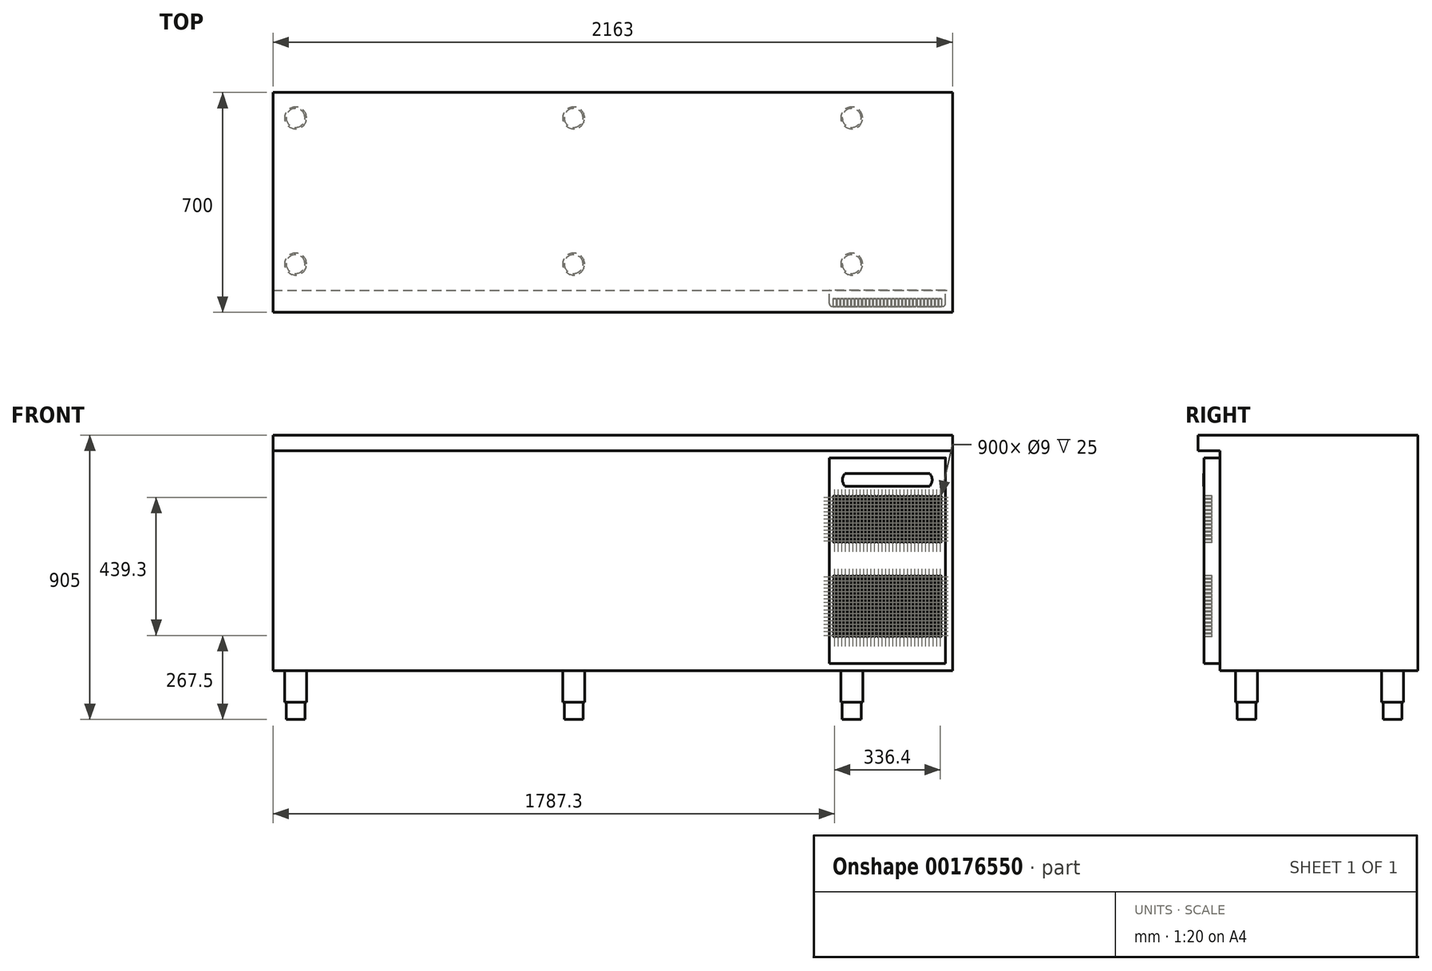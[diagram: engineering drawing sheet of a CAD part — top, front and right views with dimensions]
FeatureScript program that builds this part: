
annotation { "Feature Type Name" : "Feature", "Feature Type Description" : "" }
export const myFeature = defineFeature(function(context is Context, id is Id, definition is map)
    precondition{}
    {
        {
            var Q0;
            Q0=qCreatedBy(makeId("Top.planeOp"),FACE);
            var sketch = newSketch(context, id + "F0", { "sketchPlane" : qUnion([Q0])});
            skLineSegment(sketch, "E0.bottom", {"start": v(1081.5, 350) * mm, "end": v(-1081.5, 350) * mm});
            skLineSegment(sketch, "E0.top", {"start": v(1081.5, -350) * mm, "end": v(-1081.5, -350) * mm});
            skLineSegment(sketch, "E0.left", {"start": v(1081.5, 350) * mm, "end": v(1081.5, -350) * mm});
            skLineSegment(sketch, "E0.right", {"start": v(-1081.5, 350) * mm, "end": v(-1081.5, -350) * mm});
            skPoint(sketch, "E0.middle", {"position": v(0, 0) * mm});
            skSolve(sketch);
        }
        {
            var Q0;
            Q0 = qSketchRegion(id + "F0", true);
            extrude(context, id + "F1", {"entities" : qUnion([Q0]), "depth" : 50 * mm});
        }
        {
            var Q0;
            Q0=makeQuery(id+"F1.opExtrude","CAP_FACE",FACE,{"disambiguationData":[OSD([sQuery(id+"F0.wireOp",EDGE,"E0.bottom"),sQuery(id+"F0.wireOp",EDGE,"E0.top"),sQuery(id+"F0.wireOp",EDGE,"E0.left"),sQuery(id+"F0.wireOp",EDGE,"E0.right")])],"isStart":true});
            var sketch = newSketch(context, id + "F2", { "sketchPlane" : qUnion([Q0])});
            skLineSegment(sketch, "E1.bottom", {"start": v(-1081.5, -350) * mm, "end": v(1081.5, -350) * mm});
            skLineSegment(sketch, "E1.top", {"start": v(-1081.5, 280) * mm, "end": v(1081.5, 280) * mm});
            skLineSegment(sketch, "E1.left", {"start": v(-1081.5, -350) * mm, "end": v(-1081.5, 280) * mm});
            skLineSegment(sketch, "E1.right", {"start": v(1081.5, -350) * mm, "end": v(1081.5, 280) * mm});
            skSolve(sketch);
        }
        {
            var Q0;
            Q0 = qSketchRegion(id + "F2", true);
            extrude(context, id + "F3", {"entities" : qUnion([Q0]), "operationType" : NewBodyOperationType.ADD, "depth" : 700 * mm});
        }
        {
            var Q0;
            Q0=makeQuery(id+"F3.opExtrude","CAP_FACE",FACE,{"disambiguationData":[OSD([sQuery(id+"F2.wireOp",EDGE,"E1.bottom"),sQuery(id+"F2.wireOp",EDGE,"E1.top"),sQuery(id+"F2.wireOp",EDGE,"E1.left"),sQuery(id+"F2.wireOp",EDGE,"E1.right")])],"isStart":false});
            var sketch = newSketch(context, id + "F4", { "sketchPlane" : qUnion([Q0])});
            skCircle(sketch, "E2", {"center": v(-1009.5, 196) * mm, "radius": 35 * mm});
            skCircle(sketch, "E3", {"center": v(-124.5, 196) * mm, "radius": 35 * mm});
            skCircle(sketch, "E4", {"center": v(760.5, 196) * mm, "radius": 35 * mm});
            skCircle(sketch, "E5", {"center": v(760.5, -269) * mm, "radius": 35 * mm});
            skCircle(sketch, "E6", {"center": v(-124.5, -269) * mm, "radius": 35 * mm});
            skCircle(sketch, "E7", {"center": v(-1009.5, -269) * mm, "radius": 35 * mm});
            skSolve(sketch);
        }
        {
            var Q0;
            Q0 = qSketchRegion(id + "F4", true);
            extrude(context, id + "F5", {"entities" : qUnion([Q0]), "operationType" : NewBodyOperationType.ADD, "depth" : 100 * mm});
        }
        {
            var Q0;
            Q0=makeQuery(id+"F5.opExtrude","CAP_FACE",FACE,{"disambiguationData":[OSD([sQuery(id+"F4.wireOp",EDGE,"E2")])],"isStart":false});
            var sketch = newSketch(context, id + "F6", { "sketchPlane" : qUnion([Q0])});
            skCircle(sketch, "E8", {"center": v(-1009.5, 196) * mm, "radius": 30 * mm});
            skCircle(sketch, "E9", {"center": v(-124.5, 196) * mm, "radius": 30 * mm});
            skCircle(sketch, "E10", {"center": v(760.5, 196) * mm, "radius": 30 * mm});
            skCircle(sketch, "E11", {"center": v(760.5, -269) * mm, "radius": 30 * mm});
            skCircle(sketch, "E12", {"center": v(-124.5, -269) * mm, "radius": 30 * mm});
            skCircle(sketch, "E13", {"center": v(-1009.5, -269) * mm, "radius": 30 * mm});
            skSolve(sketch);
        }
        {
            var Q0;
            Q0 = qSketchRegion(id + "F6", true);
            extrude(context, id + "F7", {"entities" : qUnion([Q0]), "operationType" : NewBodyOperationType.ADD, "depth" : 55 * mm});
        }
        {
            var Q0;
            Q0=makeQuery(id+"F3.opExtrude","SWEPT_FACE",FACE,{"disambiguationData":[OSD([sQuery(id+"F2.wireOp",EDGE,"E1.top")])]});
            var sketch = newSketch(context, id + "F8", { "sketchPlane" : qUnion([Q0])});
            skLineSegment(sketch, "E14.bottom", {"start": v(1059, -677.5) * mm, "end": v(689, -677.5) * mm});
            skLineSegment(sketch, "E14.top", {"start": v(1059, -22.5) * mm, "end": v(689, -22.5) * mm});
            skLineSegment(sketch, "E14.left", {"start": v(1059, -677.5) * mm, "end": v(1059, -22.5) * mm});
            skLineSegment(sketch, "E14.right", {"start": v(689, -677.5) * mm, "end": v(689, -22.5) * mm});
            skSolve(sketch);
        }
        {
            var Q0;
            Q0 = qSketchRegion(id + "F8", true);
            extrude(context, id + "F9", {"entities" : qUnion([Q0]), "operationType" : NewBodyOperationType.ADD, "depth" : 51 * mm});
        }
        {
            var Q0;
            Q0=makeQuery(id+"F9.opExtrude","CAP_EDGE",EDGE,{"disambiguationData":[OSD([sQuery(id+"F8.wireOp",EDGE,"E14.right")])],"isStart":false});
            var Q1;
            Q1=makeQuery(id+"F9.opExtrude","CAP_EDGE",EDGE,{"disambiguationData":[OSD([sQuery(id+"F8.wireOp",EDGE,"E14.left")])],"isStart":false});
            fillet(context, id + "F10", {"entities" : qUnion([Q0, Q1]), "radius" : 10 * mm, "tangentPropagation" : true, "allowEdgeOverflow" : false});
        }
        {
            var Q0;
            Q0=makeQuery(id+"F9.opExtrude","CAP_FACE",FACE,{"disambiguationData":[OSD([sQuery(id+"F8.wireOp",EDGE,"E14.bottom"),sQuery(id+"F8.wireOp",EDGE,"E14.top"),sQuery(id+"F8.wireOp",EDGE,"E14.left"),sQuery(id+"F8.wireOp",EDGE,"E14.right")])],"isStart":false});
            var sketch = newSketch(context, id + "F11", { "sketchPlane" : qUnion([Q0])});
            skCircle(sketch, "E15", {"center": v(705.8, -587.5) * mm, "radius": 4.5 * mm});
            skCircle(sketch, "E16.0.1.0", {"center": v(705.8, -575.9) * mm, "radius": 4.5 * mm});
            skCircle(sketch, "E16.0.2.0", {"center": v(705.8, -564.3) * mm, "radius": 4.5 * mm});
            skCircle(sketch, "E16.0.3.0", {"center": v(705.8, -552.7) * mm, "radius": 4.5 * mm});
            skCircle(sketch, "E16.0.4.0", {"center": v(705.8, -541.1) * mm, "radius": 4.5 * mm});
            skCircle(sketch, "E16.0.5.0", {"center": v(705.8, -529.5) * mm, "radius": 4.5 * mm});
            skCircle(sketch, "E16.0.6.0", {"center": v(705.8, -517.9) * mm, "radius": 4.5 * mm});
            skCircle(sketch, "E16.0.7.0", {"center": v(705.8, -506.3) * mm, "radius": 4.5 * mm});
            skCircle(sketch, "E16.0.8.0", {"center": v(705.8, -494.7) * mm, "radius": 4.5 * mm});
            skCircle(sketch, "E16.0.9.0", {"center": v(705.8, -483.1) * mm, "radius": 4.5 * mm});
            skCircle(sketch, "E16.0.10.0", {"center": v(705.8, -471.5) * mm, "radius": 4.5 * mm});
            skCircle(sketch, "E16.0.11.0", {"center": v(705.8, -459.9) * mm, "radius": 4.5 * mm});
            skCircle(sketch, "E16.0.12.0", {"center": v(705.8, -448.3) * mm, "radius": 4.5 * mm});
            skCircle(sketch, "E16.0.13.0", {"center": v(705.8, -436.7) * mm, "radius": 4.5 * mm});
            skCircle(sketch, "E16.0.14.0", {"center": v(705.8, -425.1) * mm, "radius": 4.5 * mm});
            skCircle(sketch, "E16.0.15.0", {"center": v(705.8, -413.5) * mm, "radius": 4.5 * mm});
            skCircle(sketch, "E16.0.16.0", {"center": v(705.8, -401.9) * mm, "radius": 4.5 * mm});
            skCircle(sketch, "E16.1.0.0", {"center": v(717.4, -587.5) * mm, "radius": 4.5 * mm});
            skCircle(sketch, "E16.1.1.0", {"center": v(717.4, -575.9) * mm, "radius": 4.5 * mm});
            skCircle(sketch, "E16.1.2.0", {"center": v(717.4, -564.3) * mm, "radius": 4.5 * mm});
            skCircle(sketch, "E16.1.3.0", {"center": v(717.4, -552.7) * mm, "radius": 4.5 * mm});
            skCircle(sketch, "E16.1.4.0", {"center": v(717.4, -541.1) * mm, "radius": 4.5 * mm});
            skCircle(sketch, "E16.1.5.0", {"center": v(717.4, -529.5) * mm, "radius": 4.5 * mm});
            skCircle(sketch, "E16.1.6.0", {"center": v(717.4, -517.9) * mm, "radius": 4.5 * mm});
            skCircle(sketch, "E16.1.7.0", {"center": v(717.4, -506.3) * mm, "radius": 4.5 * mm});
            skCircle(sketch, "E16.1.8.0", {"center": v(717.4, -494.7) * mm, "radius": 4.5 * mm});
            skCircle(sketch, "E16.1.9.0", {"center": v(717.4, -483.1) * mm, "radius": 4.5 * mm});
            skCircle(sketch, "E16.1.10.0", {"center": v(717.4, -471.5) * mm, "radius": 4.5 * mm});
            skCircle(sketch, "E16.1.11.0", {"center": v(717.4, -459.9) * mm, "radius": 4.5 * mm});
            skCircle(sketch, "E16.1.12.0", {"center": v(717.4, -448.3) * mm, "radius": 4.5 * mm});
            skCircle(sketch, "E16.1.13.0", {"center": v(717.4, -436.7) * mm, "radius": 4.5 * mm});
            skCircle(sketch, "E16.1.14.0", {"center": v(717.4, -425.1) * mm, "radius": 4.5 * mm});
            skCircle(sketch, "E16.1.15.0", {"center": v(717.4, -413.5) * mm, "radius": 4.5 * mm});
            skCircle(sketch, "E16.1.16.0", {"center": v(717.4, -401.9) * mm, "radius": 4.5 * mm});
            skCircle(sketch, "E16.2.0.0", {"center": v(729, -587.5) * mm, "radius": 4.5 * mm});
            skCircle(sketch, "E16.2.1.0", {"center": v(729, -575.9) * mm, "radius": 4.5 * mm});
            skCircle(sketch, "E16.2.2.0", {"center": v(729, -564.3) * mm, "radius": 4.5 * mm});
            skCircle(sketch, "E16.2.3.0", {"center": v(729, -552.7) * mm, "radius": 4.5 * mm});
            skCircle(sketch, "E16.2.4.0", {"center": v(729, -541.1) * mm, "radius": 4.5 * mm});
            skCircle(sketch, "E16.2.5.0", {"center": v(729, -529.5) * mm, "radius": 4.5 * mm});
            skCircle(sketch, "E16.2.6.0", {"center": v(729, -517.9) * mm, "radius": 4.5 * mm});
            skCircle(sketch, "E16.2.7.0", {"center": v(729, -506.3) * mm, "radius": 4.5 * mm});
            skCircle(sketch, "E16.2.8.0", {"center": v(729, -494.7) * mm, "radius": 4.5 * mm});
            skCircle(sketch, "E16.2.9.0", {"center": v(729, -483.1) * mm, "radius": 4.5 * mm});
            skCircle(sketch, "E16.2.10.0", {"center": v(729, -471.5) * mm, "radius": 4.5 * mm});
            skCircle(sketch, "E16.2.11.0", {"center": v(729, -459.9) * mm, "radius": 4.5 * mm});
            skCircle(sketch, "E16.2.12.0", {"center": v(729, -448.3) * mm, "radius": 4.5 * mm});
            skCircle(sketch, "E16.2.13.0", {"center": v(729, -436.7) * mm, "radius": 4.5 * mm});
            skCircle(sketch, "E16.2.14.0", {"center": v(729, -425.1) * mm, "radius": 4.5 * mm});
            skCircle(sketch, "E16.2.15.0", {"center": v(729, -413.5) * mm, "radius": 4.5 * mm});
            skCircle(sketch, "E16.2.16.0", {"center": v(729, -401.9) * mm, "radius": 4.5 * mm});
            skCircle(sketch, "E16.3.0.0", {"center": v(740.6, -587.5) * mm, "radius": 4.5 * mm});
            skCircle(sketch, "E16.3.1.0", {"center": v(740.6, -575.9) * mm, "radius": 4.5 * mm});
            skCircle(sketch, "E16.3.2.0", {"center": v(740.6, -564.3) * mm, "radius": 4.5 * mm});
            skCircle(sketch, "E16.3.3.0", {"center": v(740.6, -552.7) * mm, "radius": 4.5 * mm});
            skCircle(sketch, "E16.3.4.0", {"center": v(740.6, -541.1) * mm, "radius": 4.5 * mm});
            skCircle(sketch, "E16.3.5.0", {"center": v(740.6, -529.5) * mm, "radius": 4.5 * mm});
            skCircle(sketch, "E16.3.6.0", {"center": v(740.6, -517.9) * mm, "radius": 4.5 * mm});
            skCircle(sketch, "E16.3.7.0", {"center": v(740.6, -506.3) * mm, "radius": 4.5 * mm});
            skCircle(sketch, "E16.3.8.0", {"center": v(740.6, -494.7) * mm, "radius": 4.5 * mm});
            skCircle(sketch, "E16.3.9.0", {"center": v(740.6, -483.1) * mm, "radius": 4.5 * mm});
            skCircle(sketch, "E16.3.10.0", {"center": v(740.6, -471.5) * mm, "radius": 4.5 * mm});
            skCircle(sketch, "E16.3.11.0", {"center": v(740.6, -459.9) * mm, "radius": 4.5 * mm});
            skCircle(sketch, "E16.3.12.0", {"center": v(740.6, -448.3) * mm, "radius": 4.5 * mm});
            skCircle(sketch, "E16.3.13.0", {"center": v(740.6, -436.7) * mm, "radius": 4.5 * mm});
            skCircle(sketch, "E16.3.14.0", {"center": v(740.6, -425.1) * mm, "radius": 4.5 * mm});
            skCircle(sketch, "E16.3.15.0", {"center": v(740.6, -413.5) * mm, "radius": 4.5 * mm});
            skCircle(sketch, "E16.3.16.0", {"center": v(740.6, -401.9) * mm, "radius": 4.5 * mm});
            skCircle(sketch, "E16.4.0.0", {"center": v(752.2, -587.5) * mm, "radius": 4.5 * mm});
            skCircle(sketch, "E16.4.1.0", {"center": v(752.2, -575.9) * mm, "radius": 4.5 * mm});
            skCircle(sketch, "E16.4.2.0", {"center": v(752.2, -564.3) * mm, "radius": 4.5 * mm});
            skCircle(sketch, "E16.4.3.0", {"center": v(752.2, -552.7) * mm, "radius": 4.5 * mm});
            skCircle(sketch, "E16.4.4.0", {"center": v(752.2, -541.1) * mm, "radius": 4.5 * mm});
            skCircle(sketch, "E16.4.5.0", {"center": v(752.2, -529.5) * mm, "radius": 4.5 * mm});
            skCircle(sketch, "E16.4.6.0", {"center": v(752.2, -517.9) * mm, "radius": 4.5 * mm});
            skCircle(sketch, "E16.4.7.0", {"center": v(752.2, -506.3) * mm, "radius": 4.5 * mm});
            skCircle(sketch, "E16.4.8.0", {"center": v(752.2, -494.7) * mm, "radius": 4.5 * mm});
            skCircle(sketch, "E16.4.9.0", {"center": v(752.2, -483.1) * mm, "radius": 4.5 * mm});
            skCircle(sketch, "E16.4.10.0", {"center": v(752.2, -471.5) * mm, "radius": 4.5 * mm});
            skCircle(sketch, "E16.4.11.0", {"center": v(752.2, -459.9) * mm, "radius": 4.5 * mm});
            skCircle(sketch, "E16.4.12.0", {"center": v(752.2, -448.3) * mm, "radius": 4.5 * mm});
            skCircle(sketch, "E16.4.13.0", {"center": v(752.2, -436.7) * mm, "radius": 4.5 * mm});
            skCircle(sketch, "E16.4.14.0", {"center": v(752.2, -425.1) * mm, "radius": 4.5 * mm});
            skCircle(sketch, "E16.4.15.0", {"center": v(752.2, -413.5) * mm, "radius": 4.5 * mm});
            skCircle(sketch, "E16.4.16.0", {"center": v(752.2, -401.9) * mm, "radius": 4.5 * mm});
            skCircle(sketch, "E16.5.0.0", {"center": v(763.8, -587.5) * mm, "radius": 4.5 * mm});
            skCircle(sketch, "E16.5.1.0", {"center": v(763.8, -575.9) * mm, "radius": 4.5 * mm});
            skCircle(sketch, "E16.5.2.0", {"center": v(763.8, -564.3) * mm, "radius": 4.5 * mm});
            skCircle(sketch, "E16.5.3.0", {"center": v(763.8, -552.7) * mm, "radius": 4.5 * mm});
            skCircle(sketch, "E16.5.4.0", {"center": v(763.8, -541.1) * mm, "radius": 4.5 * mm});
            skCircle(sketch, "E16.5.5.0", {"center": v(763.8, -529.5) * mm, "radius": 4.5 * mm});
            skCircle(sketch, "E16.5.6.0", {"center": v(763.8, -517.9) * mm, "radius": 4.5 * mm});
            skCircle(sketch, "E16.5.7.0", {"center": v(763.8, -506.3) * mm, "radius": 4.5 * mm});
            skCircle(sketch, "E16.5.8.0", {"center": v(763.8, -494.7) * mm, "radius": 4.5 * mm});
            skCircle(sketch, "E16.5.9.0", {"center": v(763.8, -483.1) * mm, "radius": 4.5 * mm});
            skCircle(sketch, "E16.5.10.0", {"center": v(763.8, -471.5) * mm, "radius": 4.5 * mm});
            skCircle(sketch, "E16.5.11.0", {"center": v(763.8, -459.9) * mm, "radius": 4.5 * mm});
            skCircle(sketch, "E16.5.12.0", {"center": v(763.8, -448.3) * mm, "radius": 4.5 * mm});
            skCircle(sketch, "E16.5.13.0", {"center": v(763.8, -436.7) * mm, "radius": 4.5 * mm});
            skCircle(sketch, "E16.5.14.0", {"center": v(763.8, -425.1) * mm, "radius": 4.5 * mm});
            skCircle(sketch, "E16.5.15.0", {"center": v(763.8, -413.5) * mm, "radius": 4.5 * mm});
            skCircle(sketch, "E16.5.16.0", {"center": v(763.8, -401.9) * mm, "radius": 4.5 * mm});
            skCircle(sketch, "E16.6.0.0", {"center": v(775.4, -587.5) * mm, "radius": 4.5 * mm});
            skCircle(sketch, "E16.6.1.0", {"center": v(775.4, -575.9) * mm, "radius": 4.5 * mm});
            skCircle(sketch, "E16.6.2.0", {"center": v(775.4, -564.3) * mm, "radius": 4.5 * mm});
            skCircle(sketch, "E16.6.3.0", {"center": v(775.4, -552.7) * mm, "radius": 4.5 * mm});
            skCircle(sketch, "E16.6.4.0", {"center": v(775.4, -541.1) * mm, "radius": 4.5 * mm});
            skCircle(sketch, "E16.6.5.0", {"center": v(775.4, -529.5) * mm, "radius": 4.5 * mm});
            skCircle(sketch, "E16.6.6.0", {"center": v(775.4, -517.9) * mm, "radius": 4.5 * mm});
            skCircle(sketch, "E16.6.7.0", {"center": v(775.4, -506.3) * mm, "radius": 4.5 * mm});
            skCircle(sketch, "E16.6.8.0", {"center": v(775.4, -494.7) * mm, "radius": 4.5 * mm});
            skCircle(sketch, "E16.6.9.0", {"center": v(775.4, -483.1) * mm, "radius": 4.5 * mm});
            skCircle(sketch, "E16.6.10.0", {"center": v(775.4, -471.5) * mm, "radius": 4.5 * mm});
            skCircle(sketch, "E16.6.11.0", {"center": v(775.4, -459.9) * mm, "radius": 4.5 * mm});
            skCircle(sketch, "E16.6.12.0", {"center": v(775.4, -448.3) * mm, "radius": 4.5 * mm});
            skCircle(sketch, "E16.6.13.0", {"center": v(775.4, -436.7) * mm, "radius": 4.5 * mm});
            skCircle(sketch, "E16.6.14.0", {"center": v(775.4, -425.1) * mm, "radius": 4.5 * mm});
            skCircle(sketch, "E16.6.15.0", {"center": v(775.4, -413.5) * mm, "radius": 4.5 * mm});
            skCircle(sketch, "E16.6.16.0", {"center": v(775.4, -401.9) * mm, "radius": 4.5 * mm});
            skCircle(sketch, "E16.7.0.0", {"center": v(787, -587.5) * mm, "radius": 4.5 * mm});
            skCircle(sketch, "E16.7.1.0", {"center": v(787, -575.9) * mm, "radius": 4.5 * mm});
            skCircle(sketch, "E16.7.2.0", {"center": v(787, -564.3) * mm, "radius": 4.5 * mm});
            skCircle(sketch, "E16.7.3.0", {"center": v(787, -552.7) * mm, "radius": 4.5 * mm});
            skCircle(sketch, "E16.7.4.0", {"center": v(787, -541.1) * mm, "radius": 4.5 * mm});
            skCircle(sketch, "E16.7.5.0", {"center": v(787, -529.5) * mm, "radius": 4.5 * mm});
            skCircle(sketch, "E16.7.6.0", {"center": v(787, -517.9) * mm, "radius": 4.5 * mm});
            skCircle(sketch, "E16.7.7.0", {"center": v(787, -506.3) * mm, "radius": 4.5 * mm});
            skCircle(sketch, "E16.7.8.0", {"center": v(787, -494.7) * mm, "radius": 4.5 * mm});
            skCircle(sketch, "E16.7.9.0", {"center": v(787, -483.1) * mm, "radius": 4.5 * mm});
            skCircle(sketch, "E16.7.10.0", {"center": v(787, -471.5) * mm, "radius": 4.5 * mm});
            skCircle(sketch, "E16.7.11.0", {"center": v(787, -459.9) * mm, "radius": 4.5 * mm});
            skCircle(sketch, "E16.7.12.0", {"center": v(787, -448.3) * mm, "radius": 4.5 * mm});
            skCircle(sketch, "E16.7.13.0", {"center": v(787, -436.7) * mm, "radius": 4.5 * mm});
            skCircle(sketch, "E16.7.14.0", {"center": v(787, -425.1) * mm, "radius": 4.5 * mm});
            skCircle(sketch, "E16.7.15.0", {"center": v(787, -413.5) * mm, "radius": 4.5 * mm});
            skCircle(sketch, "E16.7.16.0", {"center": v(787, -401.9) * mm, "radius": 4.5 * mm});
            skCircle(sketch, "E16.8.0.0", {"center": v(798.6, -587.5) * mm, "radius": 4.5 * mm});
            skCircle(sketch, "E16.8.1.0", {"center": v(798.6, -575.9) * mm, "radius": 4.5 * mm});
            skCircle(sketch, "E16.8.2.0", {"center": v(798.6, -564.3) * mm, "radius": 4.5 * mm});
            skCircle(sketch, "E16.8.3.0", {"center": v(798.6, -552.7) * mm, "radius": 4.5 * mm});
            skCircle(sketch, "E16.8.4.0", {"center": v(798.6, -541.1) * mm, "radius": 4.5 * mm});
            skCircle(sketch, "E16.8.5.0", {"center": v(798.6, -529.5) * mm, "radius": 4.5 * mm});
            skCircle(sketch, "E16.8.6.0", {"center": v(798.6, -517.9) * mm, "radius": 4.5 * mm});
            skCircle(sketch, "E16.8.7.0", {"center": v(798.6, -506.3) * mm, "radius": 4.5 * mm});
            skCircle(sketch, "E16.8.8.0", {"center": v(798.6, -494.7) * mm, "radius": 4.5 * mm});
            skCircle(sketch, "E16.8.9.0", {"center": v(798.6, -483.1) * mm, "radius": 4.5 * mm});
            skCircle(sketch, "E16.8.10.0", {"center": v(798.6, -471.5) * mm, "radius": 4.5 * mm});
            skCircle(sketch, "E16.8.11.0", {"center": v(798.6, -459.9) * mm, "radius": 4.5 * mm});
            skCircle(sketch, "E16.8.12.0", {"center": v(798.6, -448.3) * mm, "radius": 4.5 * mm});
            skCircle(sketch, "E16.8.13.0", {"center": v(798.6, -436.7) * mm, "radius": 4.5 * mm});
            skCircle(sketch, "E16.8.14.0", {"center": v(798.6, -425.1) * mm, "radius": 4.5 * mm});
            skCircle(sketch, "E16.8.15.0", {"center": v(798.6, -413.5) * mm, "radius": 4.5 * mm});
            skCircle(sketch, "E16.8.16.0", {"center": v(798.6, -401.9) * mm, "radius": 4.5 * mm});
            skCircle(sketch, "E16.9.0.0", {"center": v(810.2, -587.5) * mm, "radius": 4.5 * mm});
            skCircle(sketch, "E16.9.1.0", {"center": v(810.2, -575.9) * mm, "radius": 4.5 * mm});
            skCircle(sketch, "E16.9.2.0", {"center": v(810.2, -564.3) * mm, "radius": 4.5 * mm});
            skCircle(sketch, "E16.9.3.0", {"center": v(810.2, -552.7) * mm, "radius": 4.5 * mm});
            skCircle(sketch, "E16.9.4.0", {"center": v(810.2, -541.1) * mm, "radius": 4.5 * mm});
            skCircle(sketch, "E16.9.5.0", {"center": v(810.2, -529.5) * mm, "radius": 4.5 * mm});
            skCircle(sketch, "E16.9.6.0", {"center": v(810.2, -517.9) * mm, "radius": 4.5 * mm});
            skCircle(sketch, "E16.9.7.0", {"center": v(810.2, -506.3) * mm, "radius": 4.5 * mm});
            skCircle(sketch, "E16.9.8.0", {"center": v(810.2, -494.7) * mm, "radius": 4.5 * mm});
            skCircle(sketch, "E16.9.9.0", {"center": v(810.2, -483.1) * mm, "radius": 4.5 * mm});
            skCircle(sketch, "E16.9.10.0", {"center": v(810.2, -471.5) * mm, "radius": 4.5 * mm});
            skCircle(sketch, "E16.9.11.0", {"center": v(810.2, -459.9) * mm, "radius": 4.5 * mm});
            skCircle(sketch, "E16.9.12.0", {"center": v(810.2, -448.3) * mm, "radius": 4.5 * mm});
            skCircle(sketch, "E16.9.13.0", {"center": v(810.2, -436.7) * mm, "radius": 4.5 * mm});
            skCircle(sketch, "E16.9.14.0", {"center": v(810.2, -425.1) * mm, "radius": 4.5 * mm});
            skCircle(sketch, "E16.9.15.0", {"center": v(810.2, -413.5) * mm, "radius": 4.5 * mm});
            skCircle(sketch, "E16.9.16.0", {"center": v(810.2, -401.9) * mm, "radius": 4.5 * mm});
            skCircle(sketch, "E16.10.0.0", {"center": v(821.8, -587.5) * mm, "radius": 4.5 * mm});
            skCircle(sketch, "E16.10.1.0", {"center": v(821.8, -575.9) * mm, "radius": 4.5 * mm});
            skCircle(sketch, "E16.10.2.0", {"center": v(821.8, -564.3) * mm, "radius": 4.5 * mm});
            skCircle(sketch, "E16.10.3.0", {"center": v(821.8, -552.7) * mm, "radius": 4.5 * mm});
            skCircle(sketch, "E16.10.4.0", {"center": v(821.8, -541.1) * mm, "radius": 4.5 * mm});
            skCircle(sketch, "E16.10.5.0", {"center": v(821.8, -529.5) * mm, "radius": 4.5 * mm});
            skCircle(sketch, "E16.10.6.0", {"center": v(821.8, -517.9) * mm, "radius": 4.5 * mm});
            skCircle(sketch, "E16.10.7.0", {"center": v(821.8, -506.3) * mm, "radius": 4.5 * mm});
            skCircle(sketch, "E16.10.8.0", {"center": v(821.8, -494.7) * mm, "radius": 4.5 * mm});
            skCircle(sketch, "E16.10.9.0", {"center": v(821.8, -483.1) * mm, "radius": 4.5 * mm});
            skCircle(sketch, "E16.10.10.0", {"center": v(821.8, -471.5) * mm, "radius": 4.5 * mm});
            skCircle(sketch, "E16.10.11.0", {"center": v(821.8, -459.9) * mm, "radius": 4.5 * mm});
            skCircle(sketch, "E16.10.12.0", {"center": v(821.8, -448.3) * mm, "radius": 4.5 * mm});
            skCircle(sketch, "E16.10.13.0", {"center": v(821.8, -436.7) * mm, "radius": 4.5 * mm});
            skCircle(sketch, "E16.10.14.0", {"center": v(821.8, -425.1) * mm, "radius": 4.5 * mm});
            skCircle(sketch, "E16.10.15.0", {"center": v(821.8, -413.5) * mm, "radius": 4.5 * mm});
            skCircle(sketch, "E16.10.16.0", {"center": v(821.8, -401.9) * mm, "radius": 4.5 * mm});
            skCircle(sketch, "E16.11.0.0", {"center": v(833.4, -587.5) * mm, "radius": 4.5 * mm});
            skCircle(sketch, "E16.11.1.0", {"center": v(833.4, -575.9) * mm, "radius": 4.5 * mm});
            skCircle(sketch, "E16.11.2.0", {"center": v(833.4, -564.3) * mm, "radius": 4.5 * mm});
            skCircle(sketch, "E16.11.3.0", {"center": v(833.4, -552.7) * mm, "radius": 4.5 * mm});
            skCircle(sketch, "E16.11.4.0", {"center": v(833.4, -541.1) * mm, "radius": 4.5 * mm});
            skCircle(sketch, "E16.11.5.0", {"center": v(833.4, -529.5) * mm, "radius": 4.5 * mm});
            skCircle(sketch, "E16.11.6.0", {"center": v(833.4, -517.9) * mm, "radius": 4.5 * mm});
            skCircle(sketch, "E16.11.7.0", {"center": v(833.4, -506.3) * mm, "radius": 4.5 * mm});
            skCircle(sketch, "E16.11.8.0", {"center": v(833.4, -494.7) * mm, "radius": 4.5 * mm});
            skCircle(sketch, "E16.11.9.0", {"center": v(833.4, -483.1) * mm, "radius": 4.5 * mm});
            skCircle(sketch, "E16.11.10.0", {"center": v(833.4, -471.5) * mm, "radius": 4.5 * mm});
            skCircle(sketch, "E16.11.11.0", {"center": v(833.4, -459.9) * mm, "radius": 4.5 * mm});
            skCircle(sketch, "E16.11.12.0", {"center": v(833.4, -448.3) * mm, "radius": 4.5 * mm});
            skCircle(sketch, "E16.11.13.0", {"center": v(833.4, -436.7) * mm, "radius": 4.5 * mm});
            skCircle(sketch, "E16.11.14.0", {"center": v(833.4, -425.1) * mm, "radius": 4.5 * mm});
            skCircle(sketch, "E16.11.15.0", {"center": v(833.4, -413.5) * mm, "radius": 4.5 * mm});
            skCircle(sketch, "E16.11.16.0", {"center": v(833.4, -401.9) * mm, "radius": 4.5 * mm});
            skCircle(sketch, "E16.12.0.0", {"center": v(845, -587.5) * mm, "radius": 4.5 * mm});
            skCircle(sketch, "E16.12.1.0", {"center": v(845, -575.9) * mm, "radius": 4.5 * mm});
            skCircle(sketch, "E16.12.2.0", {"center": v(845, -564.3) * mm, "radius": 4.5 * mm});
            skCircle(sketch, "E16.12.3.0", {"center": v(845, -552.7) * mm, "radius": 4.5 * mm});
            skCircle(sketch, "E16.12.4.0", {"center": v(845, -541.1) * mm, "radius": 4.5 * mm});
            skCircle(sketch, "E16.12.5.0", {"center": v(845, -529.5) * mm, "radius": 4.5 * mm});
            skCircle(sketch, "E16.12.6.0", {"center": v(845, -517.9) * mm, "radius": 4.5 * mm});
            skCircle(sketch, "E16.12.7.0", {"center": v(845, -506.3) * mm, "radius": 4.5 * mm});
            skCircle(sketch, "E16.12.8.0", {"center": v(845, -494.7) * mm, "radius": 4.5 * mm});
            skCircle(sketch, "E16.12.9.0", {"center": v(845, -483.1) * mm, "radius": 4.5 * mm});
            skCircle(sketch, "E16.12.10.0", {"center": v(845, -471.5) * mm, "radius": 4.5 * mm});
            skCircle(sketch, "E16.12.11.0", {"center": v(845, -459.9) * mm, "radius": 4.5 * mm});
            skCircle(sketch, "E16.12.12.0", {"center": v(845, -448.3) * mm, "radius": 4.5 * mm});
            skCircle(sketch, "E16.12.13.0", {"center": v(845, -436.7) * mm, "radius": 4.5 * mm});
            skCircle(sketch, "E16.12.14.0", {"center": v(845, -425.1) * mm, "radius": 4.5 * mm});
            skCircle(sketch, "E16.12.15.0", {"center": v(845, -413.5) * mm, "radius": 4.5 * mm});
            skCircle(sketch, "E16.12.16.0", {"center": v(845, -401.9) * mm, "radius": 4.5 * mm});
            skCircle(sketch, "E16.13.0.0", {"center": v(856.6, -587.5) * mm, "radius": 4.5 * mm});
            skCircle(sketch, "E16.13.1.0", {"center": v(856.6, -575.9) * mm, "radius": 4.5 * mm});
            skCircle(sketch, "E16.13.2.0", {"center": v(856.6, -564.3) * mm, "radius": 4.5 * mm});
            skCircle(sketch, "E16.13.3.0", {"center": v(856.6, -552.7) * mm, "radius": 4.5 * mm});
            skCircle(sketch, "E16.13.4.0", {"center": v(856.6, -541.1) * mm, "radius": 4.5 * mm});
            skCircle(sketch, "E16.13.5.0", {"center": v(856.6, -529.5) * mm, "radius": 4.5 * mm});
            skCircle(sketch, "E16.13.6.0", {"center": v(856.6, -517.9) * mm, "radius": 4.5 * mm});
            skCircle(sketch, "E16.13.7.0", {"center": v(856.6, -506.3) * mm, "radius": 4.5 * mm});
            skCircle(sketch, "E16.13.8.0", {"center": v(856.6, -494.7) * mm, "radius": 4.5 * mm});
            skCircle(sketch, "E16.13.9.0", {"center": v(856.6, -483.1) * mm, "radius": 4.5 * mm});
            skCircle(sketch, "E16.13.10.0", {"center": v(856.6, -471.5) * mm, "radius": 4.5 * mm});
            skCircle(sketch, "E16.13.11.0", {"center": v(856.6, -459.9) * mm, "radius": 4.5 * mm});
            skCircle(sketch, "E16.13.12.0", {"center": v(856.6, -448.3) * mm, "radius": 4.5 * mm});
            skCircle(sketch, "E16.13.13.0", {"center": v(856.6, -436.7) * mm, "radius": 4.5 * mm});
            skCircle(sketch, "E16.13.14.0", {"center": v(856.6, -425.1) * mm, "radius": 4.5 * mm});
            skCircle(sketch, "E16.13.15.0", {"center": v(856.6, -413.5) * mm, "radius": 4.5 * mm});
            skCircle(sketch, "E16.13.16.0", {"center": v(856.6, -401.9) * mm, "radius": 4.5 * mm});
            skCircle(sketch, "E16.14.0.0", {"center": v(868.2, -587.5) * mm, "radius": 4.5 * mm});
            skCircle(sketch, "E16.14.1.0", {"center": v(868.2, -575.9) * mm, "radius": 4.5 * mm});
            skCircle(sketch, "E16.14.2.0", {"center": v(868.2, -564.3) * mm, "radius": 4.5 * mm});
            skCircle(sketch, "E16.14.3.0", {"center": v(868.2, -552.7) * mm, "radius": 4.5 * mm});
            skCircle(sketch, "E16.14.4.0", {"center": v(868.2, -541.1) * mm, "radius": 4.5 * mm});
            skCircle(sketch, "E16.14.5.0", {"center": v(868.2, -529.5) * mm, "radius": 4.5 * mm});
            skCircle(sketch, "E16.14.6.0", {"center": v(868.2, -517.9) * mm, "radius": 4.5 * mm});
            skCircle(sketch, "E16.14.7.0", {"center": v(868.2, -506.3) * mm, "radius": 4.5 * mm});
            skCircle(sketch, "E16.14.8.0", {"center": v(868.2, -494.7) * mm, "radius": 4.5 * mm});
            skCircle(sketch, "E16.14.9.0", {"center": v(868.2, -483.1) * mm, "radius": 4.5 * mm});
            skCircle(sketch, "E16.14.10.0", {"center": v(868.2, -471.5) * mm, "radius": 4.5 * mm});
            skCircle(sketch, "E16.14.11.0", {"center": v(868.2, -459.9) * mm, "radius": 4.5 * mm});
            skCircle(sketch, "E16.14.12.0", {"center": v(868.2, -448.3) * mm, "radius": 4.5 * mm});
            skCircle(sketch, "E16.14.13.0", {"center": v(868.2, -436.7) * mm, "radius": 4.5 * mm});
            skCircle(sketch, "E16.14.14.0", {"center": v(868.2, -425.1) * mm, "radius": 4.5 * mm});
            skCircle(sketch, "E16.14.15.0", {"center": v(868.2, -413.5) * mm, "radius": 4.5 * mm});
            skCircle(sketch, "E16.14.16.0", {"center": v(868.2, -401.9) * mm, "radius": 4.5 * mm});
            skCircle(sketch, "E16.15.0.0", {"center": v(879.8, -587.5) * mm, "radius": 4.5 * mm});
            skCircle(sketch, "E16.15.1.0", {"center": v(879.8, -575.9) * mm, "radius": 4.5 * mm});
            skCircle(sketch, "E16.15.2.0", {"center": v(879.8, -564.3) * mm, "radius": 4.5 * mm});
            skCircle(sketch, "E16.15.3.0", {"center": v(879.8, -552.7) * mm, "radius": 4.5 * mm});
            skCircle(sketch, "E16.15.4.0", {"center": v(879.8, -541.1) * mm, "radius": 4.5 * mm});
            skCircle(sketch, "E16.15.5.0", {"center": v(879.8, -529.5) * mm, "radius": 4.5 * mm});
            skCircle(sketch, "E16.15.6.0", {"center": v(879.8, -517.9) * mm, "radius": 4.5 * mm});
            skCircle(sketch, "E16.15.7.0", {"center": v(879.8, -506.3) * mm, "radius": 4.5 * mm});
            skCircle(sketch, "E16.15.8.0", {"center": v(879.8, -494.7) * mm, "radius": 4.5 * mm});
            skCircle(sketch, "E16.15.9.0", {"center": v(879.8, -483.1) * mm, "radius": 4.5 * mm});
            skCircle(sketch, "E16.15.10.0", {"center": v(879.8, -471.5) * mm, "radius": 4.5 * mm});
            skCircle(sketch, "E16.15.11.0", {"center": v(879.8, -459.9) * mm, "radius": 4.5 * mm});
            skCircle(sketch, "E16.15.12.0", {"center": v(879.8, -448.3) * mm, "radius": 4.5 * mm});
            skCircle(sketch, "E16.15.13.0", {"center": v(879.8, -436.7) * mm, "radius": 4.5 * mm});
            skCircle(sketch, "E16.15.14.0", {"center": v(879.8, -425.1) * mm, "radius": 4.5 * mm});
            skCircle(sketch, "E16.15.15.0", {"center": v(879.8, -413.5) * mm, "radius": 4.5 * mm});
            skCircle(sketch, "E16.15.16.0", {"center": v(879.8, -401.9) * mm, "radius": 4.5 * mm});
            skCircle(sketch, "E16.16.0.0", {"center": v(891.4, -587.5) * mm, "radius": 4.5 * mm});
            skCircle(sketch, "E16.16.1.0", {"center": v(891.4, -575.9) * mm, "radius": 4.5 * mm});
            skCircle(sketch, "E16.16.2.0", {"center": v(891.4, -564.3) * mm, "radius": 4.5 * mm});
            skCircle(sketch, "E16.16.3.0", {"center": v(891.4, -552.7) * mm, "radius": 4.5 * mm});
            skCircle(sketch, "E16.16.4.0", {"center": v(891.4, -541.1) * mm, "radius": 4.5 * mm});
            skCircle(sketch, "E16.16.5.0", {"center": v(891.4, -529.5) * mm, "radius": 4.5 * mm});
            skCircle(sketch, "E16.16.6.0", {"center": v(891.4, -517.9) * mm, "radius": 4.5 * mm});
            skCircle(sketch, "E16.16.7.0", {"center": v(891.4, -506.3) * mm, "radius": 4.5 * mm});
            skCircle(sketch, "E16.16.8.0", {"center": v(891.4, -494.7) * mm, "radius": 4.5 * mm});
            skCircle(sketch, "E16.16.9.0", {"center": v(891.4, -483.1) * mm, "radius": 4.5 * mm});
            skCircle(sketch, "E16.16.10.0", {"center": v(891.4, -471.5) * mm, "radius": 4.5 * mm});
            skCircle(sketch, "E16.16.11.0", {"center": v(891.4, -459.9) * mm, "radius": 4.5 * mm});
            skCircle(sketch, "E16.16.12.0", {"center": v(891.4, -448.3) * mm, "radius": 4.5 * mm});
            skCircle(sketch, "E16.16.13.0", {"center": v(891.4, -436.7) * mm, "radius": 4.5 * mm});
            skCircle(sketch, "E16.16.14.0", {"center": v(891.4, -425.1) * mm, "radius": 4.5 * mm});
            skCircle(sketch, "E16.16.15.0", {"center": v(891.4, -413.5) * mm, "radius": 4.5 * mm});
            skCircle(sketch, "E16.16.16.0", {"center": v(891.4, -401.9) * mm, "radius": 4.5 * mm});
            skCircle(sketch, "E16.17.0.0", {"center": v(903, -587.5) * mm, "radius": 4.5 * mm});
            skCircle(sketch, "E16.17.1.0", {"center": v(903, -575.9) * mm, "radius": 4.5 * mm});
            skCircle(sketch, "E16.17.2.0", {"center": v(903, -564.3) * mm, "radius": 4.5 * mm});
            skCircle(sketch, "E16.17.3.0", {"center": v(903, -552.7) * mm, "radius": 4.5 * mm});
            skCircle(sketch, "E16.17.4.0", {"center": v(903, -541.1) * mm, "radius": 4.5 * mm});
            skCircle(sketch, "E16.17.5.0", {"center": v(903, -529.5) * mm, "radius": 4.5 * mm});
            skCircle(sketch, "E16.17.6.0", {"center": v(903, -517.9) * mm, "radius": 4.5 * mm});
            skCircle(sketch, "E16.17.7.0", {"center": v(903, -506.3) * mm, "radius": 4.5 * mm});
            skCircle(sketch, "E16.17.8.0", {"center": v(903, -494.7) * mm, "radius": 4.5 * mm});
            skCircle(sketch, "E16.17.9.0", {"center": v(903, -483.1) * mm, "radius": 4.5 * mm});
            skCircle(sketch, "E16.17.10.0", {"center": v(903, -471.5) * mm, "radius": 4.5 * mm});
            skCircle(sketch, "E16.17.11.0", {"center": v(903, -459.9) * mm, "radius": 4.5 * mm});
            skCircle(sketch, "E16.17.12.0", {"center": v(903, -448.3) * mm, "radius": 4.5 * mm});
            skCircle(sketch, "E16.17.13.0", {"center": v(903, -436.7) * mm, "radius": 4.5 * mm});
            skCircle(sketch, "E16.17.14.0", {"center": v(903, -425.1) * mm, "radius": 4.5 * mm});
            skCircle(sketch, "E16.17.15.0", {"center": v(903, -413.5) * mm, "radius": 4.5 * mm});
            skCircle(sketch, "E16.17.16.0", {"center": v(903, -401.9) * mm, "radius": 4.5 * mm});
            skCircle(sketch, "E16.18.0.0", {"center": v(914.6, -587.5) * mm, "radius": 4.5 * mm});
            skCircle(sketch, "E16.18.1.0", {"center": v(914.6, -575.9) * mm, "radius": 4.5 * mm});
            skCircle(sketch, "E16.18.2.0", {"center": v(914.6, -564.3) * mm, "radius": 4.5 * mm});
            skCircle(sketch, "E16.18.3.0", {"center": v(914.6, -552.7) * mm, "radius": 4.5 * mm});
            skCircle(sketch, "E16.18.4.0", {"center": v(914.6, -541.1) * mm, "radius": 4.5 * mm});
            skCircle(sketch, "E16.18.5.0", {"center": v(914.6, -529.5) * mm, "radius": 4.5 * mm});
            skCircle(sketch, "E16.18.6.0", {"center": v(914.6, -517.9) * mm, "radius": 4.5 * mm});
            skCircle(sketch, "E16.18.7.0", {"center": v(914.6, -506.3) * mm, "radius": 4.5 * mm});
            skCircle(sketch, "E16.18.8.0", {"center": v(914.6, -494.7) * mm, "radius": 4.5 * mm});
            skCircle(sketch, "E16.18.9.0", {"center": v(914.6, -483.1) * mm, "radius": 4.5 * mm});
            skCircle(sketch, "E16.18.10.0", {"center": v(914.6, -471.5) * mm, "radius": 4.5 * mm});
            skCircle(sketch, "E16.18.11.0", {"center": v(914.6, -459.9) * mm, "radius": 4.5 * mm});
            skCircle(sketch, "E16.18.12.0", {"center": v(914.6, -448.3) * mm, "radius": 4.5 * mm});
            skCircle(sketch, "E16.18.13.0", {"center": v(914.6, -436.7) * mm, "radius": 4.5 * mm});
            skCircle(sketch, "E16.18.14.0", {"center": v(914.6, -425.1) * mm, "radius": 4.5 * mm});
            skCircle(sketch, "E16.18.15.0", {"center": v(914.6, -413.5) * mm, "radius": 4.5 * mm});
            skCircle(sketch, "E16.18.16.0", {"center": v(914.6, -401.9) * mm, "radius": 4.5 * mm});
            skCircle(sketch, "E16.19.0.0", {"center": v(926.2, -587.5) * mm, "radius": 4.5 * mm});
            skCircle(sketch, "E16.19.1.0", {"center": v(926.2, -575.9) * mm, "radius": 4.5 * mm});
            skCircle(sketch, "E16.19.2.0", {"center": v(926.2, -564.3) * mm, "radius": 4.5 * mm});
            skCircle(sketch, "E16.19.3.0", {"center": v(926.2, -552.7) * mm, "radius": 4.5 * mm});
            skCircle(sketch, "E16.19.4.0", {"center": v(926.2, -541.1) * mm, "radius": 4.5 * mm});
            skCircle(sketch, "E16.19.5.0", {"center": v(926.2, -529.5) * mm, "radius": 4.5 * mm});
            skCircle(sketch, "E16.19.6.0", {"center": v(926.2, -517.9) * mm, "radius": 4.5 * mm});
            skCircle(sketch, "E16.19.7.0", {"center": v(926.2, -506.3) * mm, "radius": 4.5 * mm});
            skCircle(sketch, "E16.19.8.0", {"center": v(926.2, -494.7) * mm, "radius": 4.5 * mm});
            skCircle(sketch, "E16.19.9.0", {"center": v(926.2, -483.1) * mm, "radius": 4.5 * mm});
            skCircle(sketch, "E16.19.10.0", {"center": v(926.2, -471.5) * mm, "radius": 4.5 * mm});
            skCircle(sketch, "E16.19.11.0", {"center": v(926.2, -459.9) * mm, "radius": 4.5 * mm});
            skCircle(sketch, "E16.19.12.0", {"center": v(926.2, -448.3) * mm, "radius": 4.5 * mm});
            skCircle(sketch, "E16.19.13.0", {"center": v(926.2, -436.7) * mm, "radius": 4.5 * mm});
            skCircle(sketch, "E16.19.14.0", {"center": v(926.2, -425.1) * mm, "radius": 4.5 * mm});
            skCircle(sketch, "E16.19.15.0", {"center": v(926.2, -413.5) * mm, "radius": 4.5 * mm});
            skCircle(sketch, "E16.19.16.0", {"center": v(926.2, -401.9) * mm, "radius": 4.5 * mm});
            skCircle(sketch, "E16.20.0.0", {"center": v(937.8, -587.5) * mm, "radius": 4.5 * mm});
            skCircle(sketch, "E16.20.1.0", {"center": v(937.8, -575.9) * mm, "radius": 4.5 * mm});
            skCircle(sketch, "E16.20.2.0", {"center": v(937.8, -564.3) * mm, "radius": 4.5 * mm});
            skCircle(sketch, "E16.20.3.0", {"center": v(937.8, -552.7) * mm, "radius": 4.5 * mm});
            skCircle(sketch, "E16.20.4.0", {"center": v(937.8, -541.1) * mm, "radius": 4.5 * mm});
            skCircle(sketch, "E16.20.5.0", {"center": v(937.8, -529.5) * mm, "radius": 4.5 * mm});
            skCircle(sketch, "E16.20.6.0", {"center": v(937.8, -517.9) * mm, "radius": 4.5 * mm});
            skCircle(sketch, "E16.20.7.0", {"center": v(937.8, -506.3) * mm, "radius": 4.5 * mm});
            skCircle(sketch, "E16.20.8.0", {"center": v(937.8, -494.7) * mm, "radius": 4.5 * mm});
            skCircle(sketch, "E16.20.9.0", {"center": v(937.8, -483.1) * mm, "radius": 4.5 * mm});
            skCircle(sketch, "E16.20.10.0", {"center": v(937.8, -471.5) * mm, "radius": 4.5 * mm});
            skCircle(sketch, "E16.20.11.0", {"center": v(937.8, -459.9) * mm, "radius": 4.5 * mm});
            skCircle(sketch, "E16.20.12.0", {"center": v(937.8, -448.3) * mm, "radius": 4.5 * mm});
            skCircle(sketch, "E16.20.13.0", {"center": v(937.8, -436.7) * mm, "radius": 4.5 * mm});
            skCircle(sketch, "E16.20.14.0", {"center": v(937.8, -425.1) * mm, "radius": 4.5 * mm});
            skCircle(sketch, "E16.20.15.0", {"center": v(937.8, -413.5) * mm, "radius": 4.5 * mm});
            skCircle(sketch, "E16.20.16.0", {"center": v(937.8, -401.9) * mm, "radius": 4.5 * mm});
            skCircle(sketch, "E16.21.0.0", {"center": v(949.4, -587.5) * mm, "radius": 4.5 * mm});
            skCircle(sketch, "E16.21.1.0", {"center": v(949.4, -575.9) * mm, "radius": 4.5 * mm});
            skCircle(sketch, "E16.21.2.0", {"center": v(949.4, -564.3) * mm, "radius": 4.5 * mm});
            skCircle(sketch, "E16.21.3.0", {"center": v(949.4, -552.7) * mm, "radius": 4.5 * mm});
            skCircle(sketch, "E16.21.4.0", {"center": v(949.4, -541.1) * mm, "radius": 4.5 * mm});
            skCircle(sketch, "E16.21.5.0", {"center": v(949.4, -529.5) * mm, "radius": 4.5 * mm});
            skCircle(sketch, "E16.21.6.0", {"center": v(949.4, -517.9) * mm, "radius": 4.5 * mm});
            skCircle(sketch, "E16.21.7.0", {"center": v(949.4, -506.3) * mm, "radius": 4.5 * mm});
            skCircle(sketch, "E16.21.8.0", {"center": v(949.4, -494.7) * mm, "radius": 4.5 * mm});
            skCircle(sketch, "E16.21.9.0", {"center": v(949.4, -483.1) * mm, "radius": 4.5 * mm});
            skCircle(sketch, "E16.21.10.0", {"center": v(949.4, -471.5) * mm, "radius": 4.5 * mm});
            skCircle(sketch, "E16.21.11.0", {"center": v(949.4, -459.9) * mm, "radius": 4.5 * mm});
            skCircle(sketch, "E16.21.12.0", {"center": v(949.4, -448.3) * mm, "radius": 4.5 * mm});
            skCircle(sketch, "E16.21.13.0", {"center": v(949.4, -436.7) * mm, "radius": 4.5 * mm});
            skCircle(sketch, "E16.21.14.0", {"center": v(949.4, -425.1) * mm, "radius": 4.5 * mm});
            skCircle(sketch, "E16.21.15.0", {"center": v(949.4, -413.5) * mm, "radius": 4.5 * mm});
            skCircle(sketch, "E16.21.16.0", {"center": v(949.4, -401.9) * mm, "radius": 4.5 * mm});
            skCircle(sketch, "E16.22.0.0", {"center": v(961, -587.5) * mm, "radius": 4.5 * mm});
            skCircle(sketch, "E16.22.1.0", {"center": v(961, -575.9) * mm, "radius": 4.5 * mm});
            skCircle(sketch, "E16.22.2.0", {"center": v(961, -564.3) * mm, "radius": 4.5 * mm});
            skCircle(sketch, "E16.22.3.0", {"center": v(961, -552.7) * mm, "radius": 4.5 * mm});
            skCircle(sketch, "E16.22.4.0", {"center": v(961, -541.1) * mm, "radius": 4.5 * mm});
            skCircle(sketch, "E16.22.5.0", {"center": v(961, -529.5) * mm, "radius": 4.5 * mm});
            skCircle(sketch, "E16.22.6.0", {"center": v(961, -517.9) * mm, "radius": 4.5 * mm});
            skCircle(sketch, "E16.22.7.0", {"center": v(961, -506.3) * mm, "radius": 4.5 * mm});
            skCircle(sketch, "E16.22.8.0", {"center": v(961, -494.7) * mm, "radius": 4.5 * mm});
            skCircle(sketch, "E16.22.9.0", {"center": v(961, -483.1) * mm, "radius": 4.5 * mm});
            skCircle(sketch, "E16.22.10.0", {"center": v(961, -471.5) * mm, "radius": 4.5 * mm});
            skCircle(sketch, "E16.22.11.0", {"center": v(961, -459.9) * mm, "radius": 4.5 * mm});
            skCircle(sketch, "E16.22.12.0", {"center": v(961, -448.3) * mm, "radius": 4.5 * mm});
            skCircle(sketch, "E16.22.13.0", {"center": v(961, -436.7) * mm, "radius": 4.5 * mm});
            skCircle(sketch, "E16.22.14.0", {"center": v(961, -425.1) * mm, "radius": 4.5 * mm});
            skCircle(sketch, "E16.22.15.0", {"center": v(961, -413.5) * mm, "radius": 4.5 * mm});
            skCircle(sketch, "E16.22.16.0", {"center": v(961, -401.9) * mm, "radius": 4.5 * mm});
            skCircle(sketch, "E16.23.0.0", {"center": v(972.6, -587.5) * mm, "radius": 4.5 * mm});
            skCircle(sketch, "E16.23.1.0", {"center": v(972.6, -575.9) * mm, "radius": 4.5 * mm});
            skCircle(sketch, "E16.23.2.0", {"center": v(972.6, -564.3) * mm, "radius": 4.5 * mm});
            skCircle(sketch, "E16.23.3.0", {"center": v(972.6, -552.7) * mm, "radius": 4.5 * mm});
            skCircle(sketch, "E16.23.4.0", {"center": v(972.6, -541.1) * mm, "radius": 4.5 * mm});
            skCircle(sketch, "E16.23.5.0", {"center": v(972.6, -529.5) * mm, "radius": 4.5 * mm});
            skCircle(sketch, "E16.23.6.0", {"center": v(972.6, -517.9) * mm, "radius": 4.5 * mm});
            skCircle(sketch, "E16.23.7.0", {"center": v(972.6, -506.3) * mm, "radius": 4.5 * mm});
            skCircle(sketch, "E16.23.8.0", {"center": v(972.6, -494.7) * mm, "radius": 4.5 * mm});
            skCircle(sketch, "E16.23.9.0", {"center": v(972.6, -483.1) * mm, "radius": 4.5 * mm});
            skCircle(sketch, "E16.23.10.0", {"center": v(972.6, -471.5) * mm, "radius": 4.5 * mm});
            skCircle(sketch, "E16.23.11.0", {"center": v(972.6, -459.9) * mm, "radius": 4.5 * mm});
            skCircle(sketch, "E16.23.12.0", {"center": v(972.6, -448.3) * mm, "radius": 4.5 * mm});
            skCircle(sketch, "E16.23.13.0", {"center": v(972.6, -436.7) * mm, "radius": 4.5 * mm});
            skCircle(sketch, "E16.23.14.0", {"center": v(972.6, -425.1) * mm, "radius": 4.5 * mm});
            skCircle(sketch, "E16.23.15.0", {"center": v(972.6, -413.5) * mm, "radius": 4.5 * mm});
            skCircle(sketch, "E16.23.16.0", {"center": v(972.6, -401.9) * mm, "radius": 4.5 * mm});
            skCircle(sketch, "E16.24.0.0", {"center": v(984.2, -587.5) * mm, "radius": 4.5 * mm});
            skCircle(sketch, "E16.24.1.0", {"center": v(984.2, -575.9) * mm, "radius": 4.5 * mm});
            skCircle(sketch, "E16.24.2.0", {"center": v(984.2, -564.3) * mm, "radius": 4.5 * mm});
            skCircle(sketch, "E16.24.3.0", {"center": v(984.2, -552.7) * mm, "radius": 4.5 * mm});
            skCircle(sketch, "E16.24.4.0", {"center": v(984.2, -541.1) * mm, "radius": 4.5 * mm});
            skCircle(sketch, "E16.24.5.0", {"center": v(984.2, -529.5) * mm, "radius": 4.5 * mm});
            skCircle(sketch, "E16.24.6.0", {"center": v(984.2, -517.9) * mm, "radius": 4.5 * mm});
            skCircle(sketch, "E16.24.7.0", {"center": v(984.2, -506.3) * mm, "radius": 4.5 * mm});
            skCircle(sketch, "E16.24.8.0", {"center": v(984.2, -494.7) * mm, "radius": 4.5 * mm});
            skCircle(sketch, "E16.24.9.0", {"center": v(984.2, -483.1) * mm, "radius": 4.5 * mm});
            skCircle(sketch, "E16.24.10.0", {"center": v(984.2, -471.5) * mm, "radius": 4.5 * mm});
            skCircle(sketch, "E16.24.11.0", {"center": v(984.2, -459.9) * mm, "radius": 4.5 * mm});
            skCircle(sketch, "E16.24.12.0", {"center": v(984.2, -448.3) * mm, "radius": 4.5 * mm});
            skCircle(sketch, "E16.24.13.0", {"center": v(984.2, -436.7) * mm, "radius": 4.5 * mm});
            skCircle(sketch, "E16.24.14.0", {"center": v(984.2, -425.1) * mm, "radius": 4.5 * mm});
            skCircle(sketch, "E16.24.15.0", {"center": v(984.2, -413.5) * mm, "radius": 4.5 * mm});
            skCircle(sketch, "E16.24.16.0", {"center": v(984.2, -401.9) * mm, "radius": 4.5 * mm});
            skCircle(sketch, "E16.25.0.0", {"center": v(995.8, -587.5) * mm, "radius": 4.5 * mm});
            skCircle(sketch, "E16.25.1.0", {"center": v(995.8, -575.9) * mm, "radius": 4.5 * mm});
            skCircle(sketch, "E16.25.2.0", {"center": v(995.8, -564.3) * mm, "radius": 4.5 * mm});
            skCircle(sketch, "E16.25.3.0", {"center": v(995.8, -552.7) * mm, "radius": 4.5 * mm});
            skCircle(sketch, "E16.25.4.0", {"center": v(995.8, -541.1) * mm, "radius": 4.5 * mm});
            skCircle(sketch, "E16.25.5.0", {"center": v(995.8, -529.5) * mm, "radius": 4.5 * mm});
            skCircle(sketch, "E16.25.6.0", {"center": v(995.8, -517.9) * mm, "radius": 4.5 * mm});
            skCircle(sketch, "E16.25.7.0", {"center": v(995.8, -506.3) * mm, "radius": 4.5 * mm});
            skCircle(sketch, "E16.25.8.0", {"center": v(995.8, -494.7) * mm, "radius": 4.5 * mm});
            skCircle(sketch, "E16.25.9.0", {"center": v(995.8, -483.1) * mm, "radius": 4.5 * mm});
            skCircle(sketch, "E16.25.10.0", {"center": v(995.8, -471.5) * mm, "radius": 4.5 * mm});
            skCircle(sketch, "E16.25.11.0", {"center": v(995.8, -459.9) * mm, "radius": 4.5 * mm});
            skCircle(sketch, "E16.25.12.0", {"center": v(995.8, -448.3) * mm, "radius": 4.5 * mm});
            skCircle(sketch, "E16.25.13.0", {"center": v(995.8, -436.7) * mm, "radius": 4.5 * mm});
            skCircle(sketch, "E16.25.14.0", {"center": v(995.8, -425.1) * mm, "radius": 4.5 * mm});
            skCircle(sketch, "E16.25.15.0", {"center": v(995.8, -413.5) * mm, "radius": 4.5 * mm});
            skCircle(sketch, "E16.25.16.0", {"center": v(995.8, -401.9) * mm, "radius": 4.5 * mm});
            skCircle(sketch, "E16.26.0.0", {"center": v(1007.4, -587.5) * mm, "radius": 4.5 * mm});
            skCircle(sketch, "E16.26.1.0", {"center": v(1007.4, -575.9) * mm, "radius": 4.5 * mm});
            skCircle(sketch, "E16.26.2.0", {"center": v(1007.4, -564.3) * mm, "radius": 4.5 * mm});
            skCircle(sketch, "E16.26.3.0", {"center": v(1007.4, -552.7) * mm, "radius": 4.5 * mm});
            skCircle(sketch, "E16.26.4.0", {"center": v(1007.4, -541.1) * mm, "radius": 4.5 * mm});
            skCircle(sketch, "E16.26.5.0", {"center": v(1007.4, -529.5) * mm, "radius": 4.5 * mm});
            skCircle(sketch, "E16.26.6.0", {"center": v(1007.4, -517.9) * mm, "radius": 4.5 * mm});
            skCircle(sketch, "E16.26.7.0", {"center": v(1007.4, -506.3) * mm, "radius": 4.5 * mm});
            skCircle(sketch, "E16.26.8.0", {"center": v(1007.4, -494.7) * mm, "radius": 4.5 * mm});
            skCircle(sketch, "E16.26.9.0", {"center": v(1007.4, -483.1) * mm, "radius": 4.5 * mm});
            skCircle(sketch, "E16.26.10.0", {"center": v(1007.4, -471.5) * mm, "radius": 4.5 * mm});
            skCircle(sketch, "E16.26.11.0", {"center": v(1007.4, -459.9) * mm, "radius": 4.5 * mm});
            skCircle(sketch, "E16.26.12.0", {"center": v(1007.4, -448.3) * mm, "radius": 4.5 * mm});
            skCircle(sketch, "E16.26.13.0", {"center": v(1007.4, -436.7) * mm, "radius": 4.5 * mm});
            skCircle(sketch, "E16.26.14.0", {"center": v(1007.4, -425.1) * mm, "radius": 4.5 * mm});
            skCircle(sketch, "E16.26.15.0", {"center": v(1007.4, -413.5) * mm, "radius": 4.5 * mm});
            skCircle(sketch, "E16.26.16.0", {"center": v(1007.4, -401.9) * mm, "radius": 4.5 * mm});
            skCircle(sketch, "E16.27.0.0", {"center": v(1019, -587.5) * mm, "radius": 4.5 * mm});
            skCircle(sketch, "E16.27.1.0", {"center": v(1019, -575.9) * mm, "radius": 4.5 * mm});
            skCircle(sketch, "E16.27.2.0", {"center": v(1019, -564.3) * mm, "radius": 4.5 * mm});
            skCircle(sketch, "E16.27.3.0", {"center": v(1019, -552.7) * mm, "radius": 4.5 * mm});
            skCircle(sketch, "E16.27.4.0", {"center": v(1019, -541.1) * mm, "radius": 4.5 * mm});
            skCircle(sketch, "E16.27.5.0", {"center": v(1019, -529.5) * mm, "radius": 4.5 * mm});
            skCircle(sketch, "E16.27.6.0", {"center": v(1019, -517.9) * mm, "radius": 4.5 * mm});
            skCircle(sketch, "E16.27.7.0", {"center": v(1019, -506.3) * mm, "radius": 4.5 * mm});
            skCircle(sketch, "E16.27.8.0", {"center": v(1019, -494.7) * mm, "radius": 4.5 * mm});
            skCircle(sketch, "E16.27.9.0", {"center": v(1019, -483.1) * mm, "radius": 4.5 * mm});
            skCircle(sketch, "E16.27.10.0", {"center": v(1019, -471.5) * mm, "radius": 4.5 * mm});
            skCircle(sketch, "E16.27.11.0", {"center": v(1019, -459.9) * mm, "radius": 4.5 * mm});
            skCircle(sketch, "E16.27.12.0", {"center": v(1019, -448.3) * mm, "radius": 4.5 * mm});
            skCircle(sketch, "E16.27.13.0", {"center": v(1019, -436.7) * mm, "radius": 4.5 * mm});
            skCircle(sketch, "E16.27.14.0", {"center": v(1019, -425.1) * mm, "radius": 4.5 * mm});
            skCircle(sketch, "E16.27.15.0", {"center": v(1019, -413.5) * mm, "radius": 4.5 * mm});
            skCircle(sketch, "E16.27.16.0", {"center": v(1019, -401.9) * mm, "radius": 4.5 * mm});
            skCircle(sketch, "E16.28.0.0", {"center": v(1030.6, -587.5) * mm, "radius": 4.5 * mm});
            skCircle(sketch, "E16.28.1.0", {"center": v(1030.6, -575.9) * mm, "radius": 4.5 * mm});
            skCircle(sketch, "E16.28.2.0", {"center": v(1030.6, -564.3) * mm, "radius": 4.5 * mm});
            skCircle(sketch, "E16.28.3.0", {"center": v(1030.6, -552.7) * mm, "radius": 4.5 * mm});
            skCircle(sketch, "E16.28.4.0", {"center": v(1030.6, -541.1) * mm, "radius": 4.5 * mm});
            skCircle(sketch, "E16.28.5.0", {"center": v(1030.6, -529.5) * mm, "radius": 4.5 * mm});
            skCircle(sketch, "E16.28.6.0", {"center": v(1030.6, -517.9) * mm, "radius": 4.5 * mm});
            skCircle(sketch, "E16.28.7.0", {"center": v(1030.6, -506.3) * mm, "radius": 4.5 * mm});
            skCircle(sketch, "E16.28.8.0", {"center": v(1030.6, -494.7) * mm, "radius": 4.5 * mm});
            skCircle(sketch, "E16.28.9.0", {"center": v(1030.6, -483.1) * mm, "radius": 4.5 * mm});
            skCircle(sketch, "E16.28.10.0", {"center": v(1030.6, -471.5) * mm, "radius": 4.5 * mm});
            skCircle(sketch, "E16.28.11.0", {"center": v(1030.6, -459.9) * mm, "radius": 4.5 * mm});
            skCircle(sketch, "E16.28.12.0", {"center": v(1030.6, -448.3) * mm, "radius": 4.5 * mm});
            skCircle(sketch, "E16.28.13.0", {"center": v(1030.6, -436.7) * mm, "radius": 4.5 * mm});
            skCircle(sketch, "E16.28.14.0", {"center": v(1030.6, -425.1) * mm, "radius": 4.5 * mm});
            skCircle(sketch, "E16.28.15.0", {"center": v(1030.6, -413.5) * mm, "radius": 4.5 * mm});
            skCircle(sketch, "E16.28.16.0", {"center": v(1030.6, -401.9) * mm, "radius": 4.5 * mm});
            skCircle(sketch, "E16.29.0.0", {"center": v(1042.2, -587.5) * mm, "radius": 4.5 * mm});
            skCircle(sketch, "E16.29.1.0", {"center": v(1042.2, -575.9) * mm, "radius": 4.5 * mm});
            skCircle(sketch, "E16.29.2.0", {"center": v(1042.2, -564.3) * mm, "radius": 4.5 * mm});
            skCircle(sketch, "E16.29.3.0", {"center": v(1042.2, -552.7) * mm, "radius": 4.5 * mm});
            skCircle(sketch, "E16.29.4.0", {"center": v(1042.2, -541.1) * mm, "radius": 4.5 * mm});
            skCircle(sketch, "E16.29.5.0", {"center": v(1042.2, -529.5) * mm, "radius": 4.5 * mm});
            skCircle(sketch, "E16.29.6.0", {"center": v(1042.2, -517.9) * mm, "radius": 4.5 * mm});
            skCircle(sketch, "E16.29.7.0", {"center": v(1042.2, -506.3) * mm, "radius": 4.5 * mm});
            skCircle(sketch, "E16.29.8.0", {"center": v(1042.2, -494.7) * mm, "radius": 4.5 * mm});
            skCircle(sketch, "E16.29.9.0", {"center": v(1042.2, -483.1) * mm, "radius": 4.5 * mm});
            skCircle(sketch, "E16.29.10.0", {"center": v(1042.2, -471.5) * mm, "radius": 4.5 * mm});
            skCircle(sketch, "E16.29.11.0", {"center": v(1042.2, -459.9) * mm, "radius": 4.5 * mm});
            skCircle(sketch, "E16.29.12.0", {"center": v(1042.2, -448.3) * mm, "radius": 4.5 * mm});
            skCircle(sketch, "E16.29.13.0", {"center": v(1042.2, -436.7) * mm, "radius": 4.5 * mm});
            skCircle(sketch, "E16.29.14.0", {"center": v(1042.2, -425.1) * mm, "radius": 4.5 * mm});
            skCircle(sketch, "E16.29.15.0", {"center": v(1042.2, -413.5) * mm, "radius": 4.5 * mm});
            skCircle(sketch, "E16.29.16.0", {"center": v(1042.2, -401.9) * mm, "radius": 4.5 * mm});
            skLineSegment(sketch, "E16.direction1", {"start": v(705.8, -587.5) * mm, "end": v(717.4, -587.5) * mm, "construction": true});
            skLineSegment(sketch, "E16.direction2", {"start": v(705.8, -587.5) * mm, "end": v(705.8, -575.9) * mm, "construction": true});
            skCircle(sketch, "E17", {"center": v(705.8, -287.4) * mm, "radius": 4.5 * mm});
            skCircle(sketch, "E18.0.1.0", {"center": v(705.8, -275.8) * mm, "radius": 4.5 * mm});
            skCircle(sketch, "E18.0.2.0", {"center": v(705.8, -264.2) * mm, "radius": 4.5 * mm});
            skCircle(sketch, "E18.0.3.0", {"center": v(705.8, -252.6) * mm, "radius": 4.5 * mm});
            skCircle(sketch, "E18.0.4.0", {"center": v(705.8, -241) * mm, "radius": 4.5 * mm});
            skCircle(sketch, "E18.0.5.0", {"center": v(705.8, -229.4) * mm, "radius": 4.5 * mm});
            skCircle(sketch, "E18.0.6.0", {"center": v(705.8, -217.8) * mm, "radius": 4.5 * mm});
            skCircle(sketch, "E18.0.7.0", {"center": v(705.8, -206.2) * mm, "radius": 4.5 * mm});
            skCircle(sketch, "E18.0.8.0", {"center": v(705.8, -194.6) * mm, "radius": 4.5 * mm});
            skCircle(sketch, "E18.0.9.0", {"center": v(705.8, -183) * mm, "radius": 4.5 * mm});
            skCircle(sketch, "E18.0.10.0", {"center": v(705.8, -171.4) * mm, "radius": 4.5 * mm});
            skCircle(sketch, "E18.0.11.0", {"center": v(705.8, -159.8) * mm, "radius": 4.5 * mm});
            skCircle(sketch, "E18.0.12.0", {"center": v(705.8, -148.2) * mm, "radius": 4.5 * mm});
            skCircle(sketch, "E18.1.0.0", {"center": v(717.4, -287.4) * mm, "radius": 4.5 * mm});
            skCircle(sketch, "E18.1.1.0", {"center": v(717.4, -275.8) * mm, "radius": 4.5 * mm});
            skCircle(sketch, "E18.1.2.0", {"center": v(717.4, -264.2) * mm, "radius": 4.5 * mm});
            skCircle(sketch, "E18.1.3.0", {"center": v(717.4, -252.6) * mm, "radius": 4.5 * mm});
            skCircle(sketch, "E18.1.4.0", {"center": v(717.4, -241) * mm, "radius": 4.5 * mm});
            skCircle(sketch, "E18.1.5.0", {"center": v(717.4, -229.4) * mm, "radius": 4.5 * mm});
            skCircle(sketch, "E18.1.6.0", {"center": v(717.4, -217.8) * mm, "radius": 4.5 * mm});
            skCircle(sketch, "E18.1.7.0", {"center": v(717.4, -206.2) * mm, "radius": 4.5 * mm});
            skCircle(sketch, "E18.1.8.0", {"center": v(717.4, -194.6) * mm, "radius": 4.5 * mm});
            skCircle(sketch, "E18.1.9.0", {"center": v(717.4, -183) * mm, "radius": 4.5 * mm});
            skCircle(sketch, "E18.1.10.0", {"center": v(717.4, -171.4) * mm, "radius": 4.5 * mm});
            skCircle(sketch, "E18.1.11.0", {"center": v(717.4, -159.8) * mm, "radius": 4.5 * mm});
            skCircle(sketch, "E18.1.12.0", {"center": v(717.4, -148.2) * mm, "radius": 4.5 * mm});
            skCircle(sketch, "E18.2.0.0", {"center": v(729, -287.4) * mm, "radius": 4.5 * mm});
            skCircle(sketch, "E18.2.1.0", {"center": v(729, -275.8) * mm, "radius": 4.5 * mm});
            skCircle(sketch, "E18.2.2.0", {"center": v(729, -264.2) * mm, "radius": 4.5 * mm});
            skCircle(sketch, "E18.2.3.0", {"center": v(729, -252.6) * mm, "radius": 4.5 * mm});
            skCircle(sketch, "E18.2.4.0", {"center": v(729, -241) * mm, "radius": 4.5 * mm});
            skCircle(sketch, "E18.2.5.0", {"center": v(729, -229.4) * mm, "radius": 4.5 * mm});
            skCircle(sketch, "E18.2.6.0", {"center": v(729, -217.8) * mm, "radius": 4.5 * mm});
            skCircle(sketch, "E18.2.7.0", {"center": v(729, -206.2) * mm, "radius": 4.5 * mm});
            skCircle(sketch, "E18.2.8.0", {"center": v(729, -194.6) * mm, "radius": 4.5 * mm});
            skCircle(sketch, "E18.2.9.0", {"center": v(729, -183) * mm, "radius": 4.5 * mm});
            skCircle(sketch, "E18.2.10.0", {"center": v(729, -171.4) * mm, "radius": 4.5 * mm});
            skCircle(sketch, "E18.2.11.0", {"center": v(729, -159.8) * mm, "radius": 4.5 * mm});
            skCircle(sketch, "E18.2.12.0", {"center": v(729, -148.2) * mm, "radius": 4.5 * mm});
            skCircle(sketch, "E18.3.0.0", {"center": v(740.6, -287.4) * mm, "radius": 4.5 * mm});
            skCircle(sketch, "E18.3.1.0", {"center": v(740.6, -275.8) * mm, "radius": 4.5 * mm});
            skCircle(sketch, "E18.3.2.0", {"center": v(740.6, -264.2) * mm, "radius": 4.5 * mm});
            skCircle(sketch, "E18.3.3.0", {"center": v(740.6, -252.6) * mm, "radius": 4.5 * mm});
            skCircle(sketch, "E18.3.4.0", {"center": v(740.6, -241) * mm, "radius": 4.5 * mm});
            skCircle(sketch, "E18.3.5.0", {"center": v(740.6, -229.4) * mm, "radius": 4.5 * mm});
            skCircle(sketch, "E18.3.6.0", {"center": v(740.6, -217.8) * mm, "radius": 4.5 * mm});
            skCircle(sketch, "E18.3.7.0", {"center": v(740.6, -206.2) * mm, "radius": 4.5 * mm});
            skCircle(sketch, "E18.3.8.0", {"center": v(740.6, -194.6) * mm, "radius": 4.5 * mm});
            skCircle(sketch, "E18.3.9.0", {"center": v(740.6, -183) * mm, "radius": 4.5 * mm});
            skCircle(sketch, "E18.3.10.0", {"center": v(740.6, -171.4) * mm, "radius": 4.5 * mm});
            skCircle(sketch, "E18.3.11.0", {"center": v(740.6, -159.8) * mm, "radius": 4.5 * mm});
            skCircle(sketch, "E18.3.12.0", {"center": v(740.6, -148.2) * mm, "radius": 4.5 * mm});
            skCircle(sketch, "E18.4.0.0", {"center": v(752.2, -287.4) * mm, "radius": 4.5 * mm});
            skCircle(sketch, "E18.4.1.0", {"center": v(752.2, -275.8) * mm, "radius": 4.5 * mm});
            skCircle(sketch, "E18.4.2.0", {"center": v(752.2, -264.2) * mm, "radius": 4.5 * mm});
            skCircle(sketch, "E18.4.3.0", {"center": v(752.2, -252.6) * mm, "radius": 4.5 * mm});
            skCircle(sketch, "E18.4.4.0", {"center": v(752.2, -241) * mm, "radius": 4.5 * mm});
            skCircle(sketch, "E18.4.5.0", {"center": v(752.2, -229.4) * mm, "radius": 4.5 * mm});
            skCircle(sketch, "E18.4.6.0", {"center": v(752.2, -217.8) * mm, "radius": 4.5 * mm});
            skCircle(sketch, "E18.4.7.0", {"center": v(752.2, -206.2) * mm, "radius": 4.5 * mm});
            skCircle(sketch, "E18.4.8.0", {"center": v(752.2, -194.6) * mm, "radius": 4.5 * mm});
            skCircle(sketch, "E18.4.9.0", {"center": v(752.2, -183) * mm, "radius": 4.5 * mm});
            skCircle(sketch, "E18.4.10.0", {"center": v(752.2, -171.4) * mm, "radius": 4.5 * mm});
            skCircle(sketch, "E18.4.11.0", {"center": v(752.2, -159.8) * mm, "radius": 4.5 * mm});
            skCircle(sketch, "E18.4.12.0", {"center": v(752.2, -148.2) * mm, "radius": 4.5 * mm});
            skCircle(sketch, "E18.5.0.0", {"center": v(763.8, -287.4) * mm, "radius": 4.5 * mm});
            skCircle(sketch, "E18.5.1.0", {"center": v(763.8, -275.8) * mm, "radius": 4.5 * mm});
            skCircle(sketch, "E18.5.2.0", {"center": v(763.8, -264.2) * mm, "radius": 4.5 * mm});
            skCircle(sketch, "E18.5.3.0", {"center": v(763.8, -252.6) * mm, "radius": 4.5 * mm});
            skCircle(sketch, "E18.5.4.0", {"center": v(763.8, -241) * mm, "radius": 4.5 * mm});
            skCircle(sketch, "E18.5.5.0", {"center": v(763.8, -229.4) * mm, "radius": 4.5 * mm});
            skCircle(sketch, "E18.5.6.0", {"center": v(763.8, -217.8) * mm, "radius": 4.5 * mm});
            skCircle(sketch, "E18.5.7.0", {"center": v(763.8, -206.2) * mm, "radius": 4.5 * mm});
            skCircle(sketch, "E18.5.8.0", {"center": v(763.8, -194.6) * mm, "radius": 4.5 * mm});
            skCircle(sketch, "E18.5.9.0", {"center": v(763.8, -183) * mm, "radius": 4.5 * mm});
            skCircle(sketch, "E18.5.10.0", {"center": v(763.8, -171.4) * mm, "radius": 4.5 * mm});
            skCircle(sketch, "E18.5.11.0", {"center": v(763.8, -159.8) * mm, "radius": 4.5 * mm});
            skCircle(sketch, "E18.5.12.0", {"center": v(763.8, -148.2) * mm, "radius": 4.5 * mm});
            skCircle(sketch, "E18.6.0.0", {"center": v(775.4, -287.4) * mm, "radius": 4.5 * mm});
            skCircle(sketch, "E18.6.1.0", {"center": v(775.4, -275.8) * mm, "radius": 4.5 * mm});
            skCircle(sketch, "E18.6.2.0", {"center": v(775.4, -264.2) * mm, "radius": 4.5 * mm});
            skCircle(sketch, "E18.6.3.0", {"center": v(775.4, -252.6) * mm, "radius": 4.5 * mm});
            skCircle(sketch, "E18.6.4.0", {"center": v(775.4, -241) * mm, "radius": 4.5 * mm});
            skCircle(sketch, "E18.6.5.0", {"center": v(775.4, -229.4) * mm, "radius": 4.5 * mm});
            skCircle(sketch, "E18.6.6.0", {"center": v(775.4, -217.8) * mm, "radius": 4.5 * mm});
            skCircle(sketch, "E18.6.7.0", {"center": v(775.4, -206.2) * mm, "radius": 4.5 * mm});
            skCircle(sketch, "E18.6.8.0", {"center": v(775.4, -194.6) * mm, "radius": 4.5 * mm});
            skCircle(sketch, "E18.6.9.0", {"center": v(775.4, -183) * mm, "radius": 4.5 * mm});
            skCircle(sketch, "E18.6.10.0", {"center": v(775.4, -171.4) * mm, "radius": 4.5 * mm});
            skCircle(sketch, "E18.6.11.0", {"center": v(775.4, -159.8) * mm, "radius": 4.5 * mm});
            skCircle(sketch, "E18.6.12.0", {"center": v(775.4, -148.2) * mm, "radius": 4.5 * mm});
            skCircle(sketch, "E18.7.0.0", {"center": v(787, -287.4) * mm, "radius": 4.5 * mm});
            skCircle(sketch, "E18.7.1.0", {"center": v(787, -275.8) * mm, "radius": 4.5 * mm});
            skCircle(sketch, "E18.7.2.0", {"center": v(787, -264.2) * mm, "radius": 4.5 * mm});
            skCircle(sketch, "E18.7.3.0", {"center": v(787, -252.6) * mm, "radius": 4.5 * mm});
            skCircle(sketch, "E18.7.4.0", {"center": v(787, -241) * mm, "radius": 4.5 * mm});
            skCircle(sketch, "E18.7.5.0", {"center": v(787, -229.4) * mm, "radius": 4.5 * mm});
            skCircle(sketch, "E18.7.6.0", {"center": v(787, -217.8) * mm, "radius": 4.5 * mm});
            skCircle(sketch, "E18.7.7.0", {"center": v(787, -206.2) * mm, "radius": 4.5 * mm});
            skCircle(sketch, "E18.7.8.0", {"center": v(787, -194.6) * mm, "radius": 4.5 * mm});
            skCircle(sketch, "E18.7.9.0", {"center": v(787, -183) * mm, "radius": 4.5 * mm});
            skCircle(sketch, "E18.7.10.0", {"center": v(787, -171.4) * mm, "radius": 4.5 * mm});
            skCircle(sketch, "E18.7.11.0", {"center": v(787, -159.8) * mm, "radius": 4.5 * mm});
            skCircle(sketch, "E18.7.12.0", {"center": v(787, -148.2) * mm, "radius": 4.5 * mm});
            skCircle(sketch, "E18.8.0.0", {"center": v(798.6, -287.4) * mm, "radius": 4.5 * mm});
            skCircle(sketch, "E18.8.1.0", {"center": v(798.6, -275.8) * mm, "radius": 4.5 * mm});
            skCircle(sketch, "E18.8.2.0", {"center": v(798.6, -264.2) * mm, "radius": 4.5 * mm});
            skCircle(sketch, "E18.8.3.0", {"center": v(798.6, -252.6) * mm, "radius": 4.5 * mm});
            skCircle(sketch, "E18.8.4.0", {"center": v(798.6, -241) * mm, "radius": 4.5 * mm});
            skCircle(sketch, "E18.8.5.0", {"center": v(798.6, -229.4) * mm, "radius": 4.5 * mm});
            skCircle(sketch, "E18.8.6.0", {"center": v(798.6, -217.8) * mm, "radius": 4.5 * mm});
            skCircle(sketch, "E18.8.7.0", {"center": v(798.6, -206.2) * mm, "radius": 4.5 * mm});
            skCircle(sketch, "E18.8.8.0", {"center": v(798.6, -194.6) * mm, "radius": 4.5 * mm});
            skCircle(sketch, "E18.8.9.0", {"center": v(798.6, -183) * mm, "radius": 4.5 * mm});
            skCircle(sketch, "E18.8.10.0", {"center": v(798.6, -171.4) * mm, "radius": 4.5 * mm});
            skCircle(sketch, "E18.8.11.0", {"center": v(798.6, -159.8) * mm, "radius": 4.5 * mm});
            skCircle(sketch, "E18.8.12.0", {"center": v(798.6, -148.2) * mm, "radius": 4.5 * mm});
            skCircle(sketch, "E18.9.0.0", {"center": v(810.2, -287.4) * mm, "radius": 4.5 * mm});
            skCircle(sketch, "E18.9.1.0", {"center": v(810.2, -275.8) * mm, "radius": 4.5 * mm});
            skCircle(sketch, "E18.9.2.0", {"center": v(810.2, -264.2) * mm, "radius": 4.5 * mm});
            skCircle(sketch, "E18.9.3.0", {"center": v(810.2, -252.6) * mm, "radius": 4.5 * mm});
            skCircle(sketch, "E18.9.4.0", {"center": v(810.2, -241) * mm, "radius": 4.5 * mm});
            skCircle(sketch, "E18.9.5.0", {"center": v(810.2, -229.4) * mm, "radius": 4.5 * mm});
            skCircle(sketch, "E18.9.6.0", {"center": v(810.2, -217.8) * mm, "radius": 4.5 * mm});
            skCircle(sketch, "E18.9.7.0", {"center": v(810.2, -206.2) * mm, "radius": 4.5 * mm});
            skCircle(sketch, "E18.9.8.0", {"center": v(810.2, -194.6) * mm, "radius": 4.5 * mm});
            skCircle(sketch, "E18.9.9.0", {"center": v(810.2, -183) * mm, "radius": 4.5 * mm});
            skCircle(sketch, "E18.9.10.0", {"center": v(810.2, -171.4) * mm, "radius": 4.5 * mm});
            skCircle(sketch, "E18.9.11.0", {"center": v(810.2, -159.8) * mm, "radius": 4.5 * mm});
            skCircle(sketch, "E18.9.12.0", {"center": v(810.2, -148.2) * mm, "radius": 4.5 * mm});
            skCircle(sketch, "E18.10.0.0", {"center": v(821.8, -287.4) * mm, "radius": 4.5 * mm});
            skCircle(sketch, "E18.10.1.0", {"center": v(821.8, -275.8) * mm, "radius": 4.5 * mm});
            skCircle(sketch, "E18.10.2.0", {"center": v(821.8, -264.2) * mm, "radius": 4.5 * mm});
            skCircle(sketch, "E18.10.3.0", {"center": v(821.8, -252.6) * mm, "radius": 4.5 * mm});
            skCircle(sketch, "E18.10.4.0", {"center": v(821.8, -241) * mm, "radius": 4.5 * mm});
            skCircle(sketch, "E18.10.5.0", {"center": v(821.8, -229.4) * mm, "radius": 4.5 * mm});
            skCircle(sketch, "E18.10.6.0", {"center": v(821.8, -217.8) * mm, "radius": 4.5 * mm});
            skCircle(sketch, "E18.10.7.0", {"center": v(821.8, -206.2) * mm, "radius": 4.5 * mm});
            skCircle(sketch, "E18.10.8.0", {"center": v(821.8, -194.6) * mm, "radius": 4.5 * mm});
            skCircle(sketch, "E18.10.9.0", {"center": v(821.8, -183) * mm, "radius": 4.5 * mm});
            skCircle(sketch, "E18.10.10.0", {"center": v(821.8, -171.4) * mm, "radius": 4.5 * mm});
            skCircle(sketch, "E18.10.11.0", {"center": v(821.8, -159.8) * mm, "radius": 4.5 * mm});
            skCircle(sketch, "E18.10.12.0", {"center": v(821.8, -148.2) * mm, "radius": 4.5 * mm});
            skCircle(sketch, "E18.11.0.0", {"center": v(833.4, -287.4) * mm, "radius": 4.5 * mm});
            skCircle(sketch, "E18.11.1.0", {"center": v(833.4, -275.8) * mm, "radius": 4.5 * mm});
            skCircle(sketch, "E18.11.2.0", {"center": v(833.4, -264.2) * mm, "radius": 4.5 * mm});
            skCircle(sketch, "E18.11.3.0", {"center": v(833.4, -252.6) * mm, "radius": 4.5 * mm});
            skCircle(sketch, "E18.11.4.0", {"center": v(833.4, -241) * mm, "radius": 4.5 * mm});
            skCircle(sketch, "E18.11.5.0", {"center": v(833.4, -229.4) * mm, "radius": 4.5 * mm});
            skCircle(sketch, "E18.11.6.0", {"center": v(833.4, -217.8) * mm, "radius": 4.5 * mm});
            skCircle(sketch, "E18.11.7.0", {"center": v(833.4, -206.2) * mm, "radius": 4.5 * mm});
            skCircle(sketch, "E18.11.8.0", {"center": v(833.4, -194.6) * mm, "radius": 4.5 * mm});
            skCircle(sketch, "E18.11.9.0", {"center": v(833.4, -183) * mm, "radius": 4.5 * mm});
            skCircle(sketch, "E18.11.10.0", {"center": v(833.4, -171.4) * mm, "radius": 4.5 * mm});
            skCircle(sketch, "E18.11.11.0", {"center": v(833.4, -159.8) * mm, "radius": 4.5 * mm});
            skCircle(sketch, "E18.11.12.0", {"center": v(833.4, -148.2) * mm, "radius": 4.5 * mm});
            skCircle(sketch, "E18.12.0.0", {"center": v(845, -287.4) * mm, "radius": 4.5 * mm});
            skCircle(sketch, "E18.12.1.0", {"center": v(845, -275.8) * mm, "radius": 4.5 * mm});
            skCircle(sketch, "E18.12.2.0", {"center": v(845, -264.2) * mm, "radius": 4.5 * mm});
            skCircle(sketch, "E18.12.3.0", {"center": v(845, -252.6) * mm, "radius": 4.5 * mm});
            skCircle(sketch, "E18.12.4.0", {"center": v(845, -241) * mm, "radius": 4.5 * mm});
            skCircle(sketch, "E18.12.5.0", {"center": v(845, -229.4) * mm, "radius": 4.5 * mm});
            skCircle(sketch, "E18.12.6.0", {"center": v(845, -217.8) * mm, "radius": 4.5 * mm});
            skCircle(sketch, "E18.12.7.0", {"center": v(845, -206.2) * mm, "radius": 4.5 * mm});
            skCircle(sketch, "E18.12.8.0", {"center": v(845, -194.6) * mm, "radius": 4.5 * mm});
            skCircle(sketch, "E18.12.9.0", {"center": v(845, -183) * mm, "radius": 4.5 * mm});
            skCircle(sketch, "E18.12.10.0", {"center": v(845, -171.4) * mm, "radius": 4.5 * mm});
            skCircle(sketch, "E18.12.11.0", {"center": v(845, -159.8) * mm, "radius": 4.5 * mm});
            skCircle(sketch, "E18.12.12.0", {"center": v(845, -148.2) * mm, "radius": 4.5 * mm});
            skCircle(sketch, "E18.13.0.0", {"center": v(856.6, -287.4) * mm, "radius": 4.5 * mm});
            skCircle(sketch, "E18.13.1.0", {"center": v(856.6, -275.8) * mm, "radius": 4.5 * mm});
            skCircle(sketch, "E18.13.2.0", {"center": v(856.6, -264.2) * mm, "radius": 4.5 * mm});
            skCircle(sketch, "E18.13.3.0", {"center": v(856.6, -252.6) * mm, "radius": 4.5 * mm});
            skCircle(sketch, "E18.13.4.0", {"center": v(856.6, -241) * mm, "radius": 4.5 * mm});
            skCircle(sketch, "E18.13.5.0", {"center": v(856.6, -229.4) * mm, "radius": 4.5 * mm});
            skCircle(sketch, "E18.13.6.0", {"center": v(856.6, -217.8) * mm, "radius": 4.5 * mm});
            skCircle(sketch, "E18.13.7.0", {"center": v(856.6, -206.2) * mm, "radius": 4.5 * mm});
            skCircle(sketch, "E18.13.8.0", {"center": v(856.6, -194.6) * mm, "radius": 4.5 * mm});
            skCircle(sketch, "E18.13.9.0", {"center": v(856.6, -183) * mm, "radius": 4.5 * mm});
            skCircle(sketch, "E18.13.10.0", {"center": v(856.6, -171.4) * mm, "radius": 4.5 * mm});
            skCircle(sketch, "E18.13.11.0", {"center": v(856.6, -159.8) * mm, "radius": 4.5 * mm});
            skCircle(sketch, "E18.13.12.0", {"center": v(856.6, -148.2) * mm, "radius": 4.5 * mm});
            skCircle(sketch, "E18.14.0.0", {"center": v(868.2, -287.4) * mm, "radius": 4.5 * mm});
            skCircle(sketch, "E18.14.1.0", {"center": v(868.2, -275.8) * mm, "radius": 4.5 * mm});
            skCircle(sketch, "E18.14.2.0", {"center": v(868.2, -264.2) * mm, "radius": 4.5 * mm});
            skCircle(sketch, "E18.14.3.0", {"center": v(868.2, -252.6) * mm, "radius": 4.5 * mm});
            skCircle(sketch, "E18.14.4.0", {"center": v(868.2, -241) * mm, "radius": 4.5 * mm});
            skCircle(sketch, "E18.14.5.0", {"center": v(868.2, -229.4) * mm, "radius": 4.5 * mm});
            skCircle(sketch, "E18.14.6.0", {"center": v(868.2, -217.8) * mm, "radius": 4.5 * mm});
            skCircle(sketch, "E18.14.7.0", {"center": v(868.2, -206.2) * mm, "radius": 4.5 * mm});
            skCircle(sketch, "E18.14.8.0", {"center": v(868.2, -194.6) * mm, "radius": 4.5 * mm});
            skCircle(sketch, "E18.14.9.0", {"center": v(868.2, -183) * mm, "radius": 4.5 * mm});
            skCircle(sketch, "E18.14.10.0", {"center": v(868.2, -171.4) * mm, "radius": 4.5 * mm});
            skCircle(sketch, "E18.14.11.0", {"center": v(868.2, -159.8) * mm, "radius": 4.5 * mm});
            skCircle(sketch, "E18.14.12.0", {"center": v(868.2, -148.2) * mm, "radius": 4.5 * mm});
            skCircle(sketch, "E18.15.0.0", {"center": v(879.8, -287.4) * mm, "radius": 4.5 * mm});
            skCircle(sketch, "E18.15.1.0", {"center": v(879.8, -275.8) * mm, "radius": 4.5 * mm});
            skCircle(sketch, "E18.15.2.0", {"center": v(879.8, -264.2) * mm, "radius": 4.5 * mm});
            skCircle(sketch, "E18.15.3.0", {"center": v(879.8, -252.6) * mm, "radius": 4.5 * mm});
            skCircle(sketch, "E18.15.4.0", {"center": v(879.8, -241) * mm, "radius": 4.5 * mm});
            skCircle(sketch, "E18.15.5.0", {"center": v(879.8, -229.4) * mm, "radius": 4.5 * mm});
            skCircle(sketch, "E18.15.6.0", {"center": v(879.8, -217.8) * mm, "radius": 4.5 * mm});
            skCircle(sketch, "E18.15.7.0", {"center": v(879.8, -206.2) * mm, "radius": 4.5 * mm});
            skCircle(sketch, "E18.15.8.0", {"center": v(879.8, -194.6) * mm, "radius": 4.5 * mm});
            skCircle(sketch, "E18.15.9.0", {"center": v(879.8, -183) * mm, "radius": 4.5 * mm});
            skCircle(sketch, "E18.15.10.0", {"center": v(879.8, -171.4) * mm, "radius": 4.5 * mm});
            skCircle(sketch, "E18.15.11.0", {"center": v(879.8, -159.8) * mm, "radius": 4.5 * mm});
            skCircle(sketch, "E18.15.12.0", {"center": v(879.8, -148.2) * mm, "radius": 4.5 * mm});
            skCircle(sketch, "E18.16.0.0", {"center": v(891.4, -287.4) * mm, "radius": 4.5 * mm});
            skCircle(sketch, "E18.16.1.0", {"center": v(891.4, -275.8) * mm, "radius": 4.5 * mm});
            skCircle(sketch, "E18.16.2.0", {"center": v(891.4, -264.2) * mm, "radius": 4.5 * mm});
            skCircle(sketch, "E18.16.3.0", {"center": v(891.4, -252.6) * mm, "radius": 4.5 * mm});
            skCircle(sketch, "E18.16.4.0", {"center": v(891.4, -241) * mm, "radius": 4.5 * mm});
            skCircle(sketch, "E18.16.5.0", {"center": v(891.4, -229.4) * mm, "radius": 4.5 * mm});
            skCircle(sketch, "E18.16.6.0", {"center": v(891.4, -217.8) * mm, "radius": 4.5 * mm});
            skCircle(sketch, "E18.16.7.0", {"center": v(891.4, -206.2) * mm, "radius": 4.5 * mm});
            skCircle(sketch, "E18.16.8.0", {"center": v(891.4, -194.6) * mm, "radius": 4.5 * mm});
            skCircle(sketch, "E18.16.9.0", {"center": v(891.4, -183) * mm, "radius": 4.5 * mm});
            skCircle(sketch, "E18.16.10.0", {"center": v(891.4, -171.4) * mm, "radius": 4.5 * mm});
            skCircle(sketch, "E18.16.11.0", {"center": v(891.4, -159.8) * mm, "radius": 4.5 * mm});
            skCircle(sketch, "E18.16.12.0", {"center": v(891.4, -148.2) * mm, "radius": 4.5 * mm});
            skCircle(sketch, "E18.17.0.0", {"center": v(903, -287.4) * mm, "radius": 4.5 * mm});
            skCircle(sketch, "E18.17.1.0", {"center": v(903, -275.8) * mm, "radius": 4.5 * mm});
            skCircle(sketch, "E18.17.2.0", {"center": v(903, -264.2) * mm, "radius": 4.5 * mm});
            skCircle(sketch, "E18.17.3.0", {"center": v(903, -252.6) * mm, "radius": 4.5 * mm});
            skCircle(sketch, "E18.17.4.0", {"center": v(903, -241) * mm, "radius": 4.5 * mm});
            skCircle(sketch, "E18.17.5.0", {"center": v(903, -229.4) * mm, "radius": 4.5 * mm});
            skCircle(sketch, "E18.17.6.0", {"center": v(903, -217.8) * mm, "radius": 4.5 * mm});
            skCircle(sketch, "E18.17.7.0", {"center": v(903, -206.2) * mm, "radius": 4.5 * mm});
            skCircle(sketch, "E18.17.8.0", {"center": v(903, -194.6) * mm, "radius": 4.5 * mm});
            skCircle(sketch, "E18.17.9.0", {"center": v(903, -183) * mm, "radius": 4.5 * mm});
            skCircle(sketch, "E18.17.10.0", {"center": v(903, -171.4) * mm, "radius": 4.5 * mm});
            skCircle(sketch, "E18.17.11.0", {"center": v(903, -159.8) * mm, "radius": 4.5 * mm});
            skCircle(sketch, "E18.17.12.0", {"center": v(903, -148.2) * mm, "radius": 4.5 * mm});
            skCircle(sketch, "E18.18.0.0", {"center": v(914.6, -287.4) * mm, "radius": 4.5 * mm});
            skCircle(sketch, "E18.18.1.0", {"center": v(914.6, -275.8) * mm, "radius": 4.5 * mm});
            skCircle(sketch, "E18.18.2.0", {"center": v(914.6, -264.2) * mm, "radius": 4.5 * mm});
            skCircle(sketch, "E18.18.3.0", {"center": v(914.6, -252.6) * mm, "radius": 4.5 * mm});
            skCircle(sketch, "E18.18.4.0", {"center": v(914.6, -241) * mm, "radius": 4.5 * mm});
            skCircle(sketch, "E18.18.5.0", {"center": v(914.6, -229.4) * mm, "radius": 4.5 * mm});
            skCircle(sketch, "E18.18.6.0", {"center": v(914.6, -217.8) * mm, "radius": 4.5 * mm});
            skCircle(sketch, "E18.18.7.0", {"center": v(914.6, -206.2) * mm, "radius": 4.5 * mm});
            skCircle(sketch, "E18.18.8.0", {"center": v(914.6, -194.6) * mm, "radius": 4.5 * mm});
            skCircle(sketch, "E18.18.9.0", {"center": v(914.6, -183) * mm, "radius": 4.5 * mm});
            skCircle(sketch, "E18.18.10.0", {"center": v(914.6, -171.4) * mm, "radius": 4.5 * mm});
            skCircle(sketch, "E18.18.11.0", {"center": v(914.6, -159.8) * mm, "radius": 4.5 * mm});
            skCircle(sketch, "E18.18.12.0", {"center": v(914.6, -148.2) * mm, "radius": 4.5 * mm});
            skCircle(sketch, "E18.19.0.0", {"center": v(926.2, -287.4) * mm, "radius": 4.5 * mm});
            skCircle(sketch, "E18.19.1.0", {"center": v(926.2, -275.8) * mm, "radius": 4.5 * mm});
            skCircle(sketch, "E18.19.2.0", {"center": v(926.2, -264.2) * mm, "radius": 4.5 * mm});
            skCircle(sketch, "E18.19.3.0", {"center": v(926.2, -252.6) * mm, "radius": 4.5 * mm});
            skCircle(sketch, "E18.19.4.0", {"center": v(926.2, -241) * mm, "radius": 4.5 * mm});
            skCircle(sketch, "E18.19.5.0", {"center": v(926.2, -229.4) * mm, "radius": 4.5 * mm});
            skCircle(sketch, "E18.19.6.0", {"center": v(926.2, -217.8) * mm, "radius": 4.5 * mm});
            skCircle(sketch, "E18.19.7.0", {"center": v(926.2, -206.2) * mm, "radius": 4.5 * mm});
            skCircle(sketch, "E18.19.8.0", {"center": v(926.2, -194.6) * mm, "radius": 4.5 * mm});
            skCircle(sketch, "E18.19.9.0", {"center": v(926.2, -183) * mm, "radius": 4.5 * mm});
            skCircle(sketch, "E18.19.10.0", {"center": v(926.2, -171.4) * mm, "radius": 4.5 * mm});
            skCircle(sketch, "E18.19.11.0", {"center": v(926.2, -159.8) * mm, "radius": 4.5 * mm});
            skCircle(sketch, "E18.19.12.0", {"center": v(926.2, -148.2) * mm, "radius": 4.5 * mm});
            skCircle(sketch, "E18.20.0.0", {"center": v(937.8, -287.4) * mm, "radius": 4.5 * mm});
            skCircle(sketch, "E18.20.1.0", {"center": v(937.8, -275.8) * mm, "radius": 4.5 * mm});
            skCircle(sketch, "E18.20.2.0", {"center": v(937.8, -264.2) * mm, "radius": 4.5 * mm});
            skCircle(sketch, "E18.20.3.0", {"center": v(937.8, -252.6) * mm, "radius": 4.5 * mm});
            skCircle(sketch, "E18.20.4.0", {"center": v(937.8, -241) * mm, "radius": 4.5 * mm});
            skCircle(sketch, "E18.20.5.0", {"center": v(937.8, -229.4) * mm, "radius": 4.5 * mm});
            skCircle(sketch, "E18.20.6.0", {"center": v(937.8, -217.8) * mm, "radius": 4.5 * mm});
            skCircle(sketch, "E18.20.7.0", {"center": v(937.8, -206.2) * mm, "radius": 4.5 * mm});
            skCircle(sketch, "E18.20.8.0", {"center": v(937.8, -194.6) * mm, "radius": 4.5 * mm});
            skCircle(sketch, "E18.20.9.0", {"center": v(937.8, -183) * mm, "radius": 4.5 * mm});
            skCircle(sketch, "E18.20.10.0", {"center": v(937.8, -171.4) * mm, "radius": 4.5 * mm});
            skCircle(sketch, "E18.20.11.0", {"center": v(937.8, -159.8) * mm, "radius": 4.5 * mm});
            skCircle(sketch, "E18.20.12.0", {"center": v(937.8, -148.2) * mm, "radius": 4.5 * mm});
            skCircle(sketch, "E18.21.0.0", {"center": v(949.4, -287.4) * mm, "radius": 4.5 * mm});
            skCircle(sketch, "E18.21.1.0", {"center": v(949.4, -275.8) * mm, "radius": 4.5 * mm});
            skCircle(sketch, "E18.21.2.0", {"center": v(949.4, -264.2) * mm, "radius": 4.5 * mm});
            skCircle(sketch, "E18.21.3.0", {"center": v(949.4, -252.6) * mm, "radius": 4.5 * mm});
            skCircle(sketch, "E18.21.4.0", {"center": v(949.4, -241) * mm, "radius": 4.5 * mm});
            skCircle(sketch, "E18.21.5.0", {"center": v(949.4, -229.4) * mm, "radius": 4.5 * mm});
            skCircle(sketch, "E18.21.6.0", {"center": v(949.4, -217.8) * mm, "radius": 4.5 * mm});
            skCircle(sketch, "E18.21.7.0", {"center": v(949.4, -206.2) * mm, "radius": 4.5 * mm});
            skCircle(sketch, "E18.21.8.0", {"center": v(949.4, -194.6) * mm, "radius": 4.5 * mm});
            skCircle(sketch, "E18.21.9.0", {"center": v(949.4, -183) * mm, "radius": 4.5 * mm});
            skCircle(sketch, "E18.21.10.0", {"center": v(949.4, -171.4) * mm, "radius": 4.5 * mm});
            skCircle(sketch, "E18.21.11.0", {"center": v(949.4, -159.8) * mm, "radius": 4.5 * mm});
            skCircle(sketch, "E18.21.12.0", {"center": v(949.4, -148.2) * mm, "radius": 4.5 * mm});
            skCircle(sketch, "E18.22.0.0", {"center": v(961, -287.4) * mm, "radius": 4.5 * mm});
            skCircle(sketch, "E18.22.1.0", {"center": v(961, -275.8) * mm, "radius": 4.5 * mm});
            skCircle(sketch, "E18.22.2.0", {"center": v(961, -264.2) * mm, "radius": 4.5 * mm});
            skCircle(sketch, "E18.22.3.0", {"center": v(961, -252.6) * mm, "radius": 4.5 * mm});
            skCircle(sketch, "E18.22.4.0", {"center": v(961, -241) * mm, "radius": 4.5 * mm});
            skCircle(sketch, "E18.22.5.0", {"center": v(961, -229.4) * mm, "radius": 4.5 * mm});
            skCircle(sketch, "E18.22.6.0", {"center": v(961, -217.8) * mm, "radius": 4.5 * mm});
            skCircle(sketch, "E18.22.7.0", {"center": v(961, -206.2) * mm, "radius": 4.5 * mm});
            skCircle(sketch, "E18.22.8.0", {"center": v(961, -194.6) * mm, "radius": 4.5 * mm});
            skCircle(sketch, "E18.22.9.0", {"center": v(961, -183) * mm, "radius": 4.5 * mm});
            skCircle(sketch, "E18.22.10.0", {"center": v(961, -171.4) * mm, "radius": 4.5 * mm});
            skCircle(sketch, "E18.22.11.0", {"center": v(961, -159.8) * mm, "radius": 4.5 * mm});
            skCircle(sketch, "E18.22.12.0", {"center": v(961, -148.2) * mm, "radius": 4.5 * mm});
            skCircle(sketch, "E18.23.0.0", {"center": v(972.6, -287.4) * mm, "radius": 4.5 * mm});
            skCircle(sketch, "E18.23.1.0", {"center": v(972.6, -275.8) * mm, "radius": 4.5 * mm});
            skCircle(sketch, "E18.23.2.0", {"center": v(972.6, -264.2) * mm, "radius": 4.5 * mm});
            skCircle(sketch, "E18.23.3.0", {"center": v(972.6, -252.6) * mm, "radius": 4.5 * mm});
            skCircle(sketch, "E18.23.4.0", {"center": v(972.6, -241) * mm, "radius": 4.5 * mm});
            skCircle(sketch, "E18.23.5.0", {"center": v(972.6, -229.4) * mm, "radius": 4.5 * mm});
            skCircle(sketch, "E18.23.6.0", {"center": v(972.6, -217.8) * mm, "radius": 4.5 * mm});
            skCircle(sketch, "E18.23.7.0", {"center": v(972.6, -206.2) * mm, "radius": 4.5 * mm});
            skCircle(sketch, "E18.23.8.0", {"center": v(972.6, -194.6) * mm, "radius": 4.5 * mm});
            skCircle(sketch, "E18.23.9.0", {"center": v(972.6, -183) * mm, "radius": 4.5 * mm});
            skCircle(sketch, "E18.23.10.0", {"center": v(972.6, -171.4) * mm, "radius": 4.5 * mm});
            skCircle(sketch, "E18.23.11.0", {"center": v(972.6, -159.8) * mm, "radius": 4.5 * mm});
            skCircle(sketch, "E18.23.12.0", {"center": v(972.6, -148.2) * mm, "radius": 4.5 * mm});
            skCircle(sketch, "E18.24.0.0", {"center": v(984.2, -287.4) * mm, "radius": 4.5 * mm});
            skCircle(sketch, "E18.24.1.0", {"center": v(984.2, -275.8) * mm, "radius": 4.5 * mm});
            skCircle(sketch, "E18.24.2.0", {"center": v(984.2, -264.2) * mm, "radius": 4.5 * mm});
            skCircle(sketch, "E18.24.3.0", {"center": v(984.2, -252.6) * mm, "radius": 4.5 * mm});
            skCircle(sketch, "E18.24.4.0", {"center": v(984.2, -241) * mm, "radius": 4.5 * mm});
            skCircle(sketch, "E18.24.5.0", {"center": v(984.2, -229.4) * mm, "radius": 4.5 * mm});
            skCircle(sketch, "E18.24.6.0", {"center": v(984.2, -217.8) * mm, "radius": 4.5 * mm});
            skCircle(sketch, "E18.24.7.0", {"center": v(984.2, -206.2) * mm, "radius": 4.5 * mm});
            skCircle(sketch, "E18.24.8.0", {"center": v(984.2, -194.6) * mm, "radius": 4.5 * mm});
            skCircle(sketch, "E18.24.9.0", {"center": v(984.2, -183) * mm, "radius": 4.5 * mm});
            skCircle(sketch, "E18.24.10.0", {"center": v(984.2, -171.4) * mm, "radius": 4.5 * mm});
            skCircle(sketch, "E18.24.11.0", {"center": v(984.2, -159.8) * mm, "radius": 4.5 * mm});
            skCircle(sketch, "E18.24.12.0", {"center": v(984.2, -148.2) * mm, "radius": 4.5 * mm});
            skCircle(sketch, "E18.25.0.0", {"center": v(995.8, -287.4) * mm, "radius": 4.5 * mm});
            skCircle(sketch, "E18.25.1.0", {"center": v(995.8, -275.8) * mm, "radius": 4.5 * mm});
            skCircle(sketch, "E18.25.2.0", {"center": v(995.8, -264.2) * mm, "radius": 4.5 * mm});
            skCircle(sketch, "E18.25.3.0", {"center": v(995.8, -252.6) * mm, "radius": 4.5 * mm});
            skCircle(sketch, "E18.25.4.0", {"center": v(995.8, -241) * mm, "radius": 4.5 * mm});
            skCircle(sketch, "E18.25.5.0", {"center": v(995.8, -229.4) * mm, "radius": 4.5 * mm});
            skCircle(sketch, "E18.25.6.0", {"center": v(995.8, -217.8) * mm, "radius": 4.5 * mm});
            skCircle(sketch, "E18.25.7.0", {"center": v(995.8, -206.2) * mm, "radius": 4.5 * mm});
            skCircle(sketch, "E18.25.8.0", {"center": v(995.8, -194.6) * mm, "radius": 4.5 * mm});
            skCircle(sketch, "E18.25.9.0", {"center": v(995.8, -183) * mm, "radius": 4.5 * mm});
            skCircle(sketch, "E18.25.10.0", {"center": v(995.8, -171.4) * mm, "radius": 4.5 * mm});
            skCircle(sketch, "E18.25.11.0", {"center": v(995.8, -159.8) * mm, "radius": 4.5 * mm});
            skCircle(sketch, "E18.25.12.0", {"center": v(995.8, -148.2) * mm, "radius": 4.5 * mm});
            skCircle(sketch, "E18.26.0.0", {"center": v(1007.4, -287.4) * mm, "radius": 4.5 * mm});
            skCircle(sketch, "E18.26.1.0", {"center": v(1007.4, -275.8) * mm, "radius": 4.5 * mm});
            skCircle(sketch, "E18.26.2.0", {"center": v(1007.4, -264.2) * mm, "radius": 4.5 * mm});
            skCircle(sketch, "E18.26.3.0", {"center": v(1007.4, -252.6) * mm, "radius": 4.5 * mm});
            skCircle(sketch, "E18.26.4.0", {"center": v(1007.4, -241) * mm, "radius": 4.5 * mm});
            skCircle(sketch, "E18.26.5.0", {"center": v(1007.4, -229.4) * mm, "radius": 4.5 * mm});
            skCircle(sketch, "E18.26.6.0", {"center": v(1007.4, -217.8) * mm, "radius": 4.5 * mm});
            skCircle(sketch, "E18.26.7.0", {"center": v(1007.4, -206.2) * mm, "radius": 4.5 * mm});
            skCircle(sketch, "E18.26.8.0", {"center": v(1007.4, -194.6) * mm, "radius": 4.5 * mm});
            skCircle(sketch, "E18.26.9.0", {"center": v(1007.4, -183) * mm, "radius": 4.5 * mm});
            skCircle(sketch, "E18.26.10.0", {"center": v(1007.4, -171.4) * mm, "radius": 4.5 * mm});
            skCircle(sketch, "E18.26.11.0", {"center": v(1007.4, -159.8) * mm, "radius": 4.5 * mm});
            skCircle(sketch, "E18.26.12.0", {"center": v(1007.4, -148.2) * mm, "radius": 4.5 * mm});
            skCircle(sketch, "E18.27.0.0", {"center": v(1019, -287.4) * mm, "radius": 4.5 * mm});
            skCircle(sketch, "E18.27.1.0", {"center": v(1019, -275.8) * mm, "radius": 4.5 * mm});
            skCircle(sketch, "E18.27.2.0", {"center": v(1019, -264.2) * mm, "radius": 4.5 * mm});
            skCircle(sketch, "E18.27.3.0", {"center": v(1019, -252.6) * mm, "radius": 4.5 * mm});
            skCircle(sketch, "E18.27.4.0", {"center": v(1019, -241) * mm, "radius": 4.5 * mm});
            skCircle(sketch, "E18.27.5.0", {"center": v(1019, -229.4) * mm, "radius": 4.5 * mm});
            skCircle(sketch, "E18.27.6.0", {"center": v(1019, -217.8) * mm, "radius": 4.5 * mm});
            skCircle(sketch, "E18.27.7.0", {"center": v(1019, -206.2) * mm, "radius": 4.5 * mm});
            skCircle(sketch, "E18.27.8.0", {"center": v(1019, -194.6) * mm, "radius": 4.5 * mm});
            skCircle(sketch, "E18.27.9.0", {"center": v(1019, -183) * mm, "radius": 4.5 * mm});
            skCircle(sketch, "E18.27.10.0", {"center": v(1019, -171.4) * mm, "radius": 4.5 * mm});
            skCircle(sketch, "E18.27.11.0", {"center": v(1019, -159.8) * mm, "radius": 4.5 * mm});
            skCircle(sketch, "E18.27.12.0", {"center": v(1019, -148.2) * mm, "radius": 4.5 * mm});
            skCircle(sketch, "E18.28.0.0", {"center": v(1030.6, -287.4) * mm, "radius": 4.5 * mm});
            skCircle(sketch, "E18.28.1.0", {"center": v(1030.6, -275.8) * mm, "radius": 4.5 * mm});
            skCircle(sketch, "E18.28.2.0", {"center": v(1030.6, -264.2) * mm, "radius": 4.5 * mm});
            skCircle(sketch, "E18.28.3.0", {"center": v(1030.6, -252.6) * mm, "radius": 4.5 * mm});
            skCircle(sketch, "E18.28.4.0", {"center": v(1030.6, -241) * mm, "radius": 4.5 * mm});
            skCircle(sketch, "E18.28.5.0", {"center": v(1030.6, -229.4) * mm, "radius": 4.5 * mm});
            skCircle(sketch, "E18.28.6.0", {"center": v(1030.6, -217.8) * mm, "radius": 4.5 * mm});
            skCircle(sketch, "E18.28.7.0", {"center": v(1030.6, -206.2) * mm, "radius": 4.5 * mm});
            skCircle(sketch, "E18.28.8.0", {"center": v(1030.6, -194.6) * mm, "radius": 4.5 * mm});
            skCircle(sketch, "E18.28.9.0", {"center": v(1030.6, -183) * mm, "radius": 4.5 * mm});
            skCircle(sketch, "E18.28.10.0", {"center": v(1030.6, -171.4) * mm, "radius": 4.5 * mm});
            skCircle(sketch, "E18.28.11.0", {"center": v(1030.6, -159.8) * mm, "radius": 4.5 * mm});
            skCircle(sketch, "E18.28.12.0", {"center": v(1030.6, -148.2) * mm, "radius": 4.5 * mm});
            skCircle(sketch, "E18.29.0.0", {"center": v(1042.2, -287.4) * mm, "radius": 4.5 * mm});
            skCircle(sketch, "E18.29.1.0", {"center": v(1042.2, -275.8) * mm, "radius": 4.5 * mm});
            skCircle(sketch, "E18.29.2.0", {"center": v(1042.2, -264.2) * mm, "radius": 4.5 * mm});
            skCircle(sketch, "E18.29.3.0", {"center": v(1042.2, -252.6) * mm, "radius": 4.5 * mm});
            skCircle(sketch, "E18.29.4.0", {"center": v(1042.2, -241) * mm, "radius": 4.5 * mm});
            skCircle(sketch, "E18.29.5.0", {"center": v(1042.2, -229.4) * mm, "radius": 4.5 * mm});
            skCircle(sketch, "E18.29.6.0", {"center": v(1042.2, -217.8) * mm, "radius": 4.5 * mm});
            skCircle(sketch, "E18.29.7.0", {"center": v(1042.2, -206.2) * mm, "radius": 4.5 * mm});
            skCircle(sketch, "E18.29.8.0", {"center": v(1042.2, -194.6) * mm, "radius": 4.5 * mm});
            skCircle(sketch, "E18.29.9.0", {"center": v(1042.2, -183) * mm, "radius": 4.5 * mm});
            skCircle(sketch, "E18.29.10.0", {"center": v(1042.2, -171.4) * mm, "radius": 4.5 * mm});
            skCircle(sketch, "E18.29.11.0", {"center": v(1042.2, -159.8) * mm, "radius": 4.5 * mm});
            skCircle(sketch, "E18.29.12.0", {"center": v(1042.2, -148.2) * mm, "radius": 4.5 * mm});
            skLineSegment(sketch, "E18.direction1", {"start": v(705.8, -287.4) * mm, "end": v(717.4, -287.4) * mm, "construction": true});
            skLineSegment(sketch, "E18.direction2", {"start": v(705.8, -287.4) * mm, "end": v(705.8, -275.8) * mm, "construction": true});
            skSolve(sketch);
        }
        {
            var Q0;
            Q0 = qSketchRegion(id + "F11", true);
            extrude(context, id + "F12", {"entities" : qUnion([Q0]), "operationType" : NewBodyOperationType.REMOVE, "oppositeDirection" : true, "depth" : 25 * mm});
        }
        {
            var Q0;
            Q0=makeQuery(id+"F9.opExtrude","CAP_FACE",FACE,{"disambiguationData":[OSD([sQuery(id+"F8.wireOp",EDGE,"E14.bottom"),sQuery(id+"F8.wireOp",EDGE,"E14.top"),sQuery(id+"F8.wireOp",EDGE,"E14.left"),sQuery(id+"F8.wireOp",EDGE,"E14.right")])],"isStart":false});
            var sketch = newSketch(context, id + "F13", { "sketchPlane" : qUnion([Q0])});
            skLineSegment(sketch, "E19.bottom", {"start": v(739, -72.5) * mm, "end": v(1009, -72.5) * mm});
            skLineSegment(sketch, "E19.top", {"start": v(739, -112.5) * mm, "end": v(1009, -112.5) * mm});
            skLineSegment(sketch, "E19.left", {"start": v(739, -72.5) * mm, "end": v(739, -112.5) * mm});
            skLineSegment(sketch, "E19.right", {"start": v(1009, -72.5) * mm, "end": v(1009, -112.5) * mm});
            skArc(sketch, "E20", {"start": v(739, -112.5) * mm, "mid": v(731.36, -92.5) * mm, "end": v(739, -72.5) * mm});
            skPoint(sketch, "E20.centerSnap0", {"position": v(739, -92.5) * mm});
            skLineSegment(sketch, "E21", {"start": v(874, -72.5) * mm, "end": v(874, -112.5) * mm, "construction": true});
            skArc(sketch, "E22.MirrorCS", {"start": v(1009, -112.5) * mm, "mid": v(1016.64, -92.5) * mm, "end": v(1009, -72.5) * mm});
            skSolve(sketch);
        }
        {
            var Q0;
            Q0 = qSketchRegion(id + "F13", true);
            extrude(context, id + "F14", {"entities" : qUnion([Q0]), "depth" : 1 * mm});
        }
    });
